annotation { "Feature Type Name" : "Feature", "Feature Type Description" : "" }
export const myFeature = defineFeature(function(context is Context, id is Id, definition is map)
    precondition{}
    {
        {
            var Q0;
            Q0=qCreatedBy(makeId("Top.planeOp"),FACE);
            var sketch = newSketch(context, id + "F0", { "sketchPlane" : qUnion([Q0])});
            skLineSegment(sketch, "E0.bottom", {"start": v(-60, -117) * mm, "end": v(60, -117) * mm});
            skLineSegment(sketch, "E0.left", {"start": v(-60, -117) * mm, "end": v(-60, 59) * mm});
            skLineSegment(sketch, "E0.right", {"start": v(60, -117) * mm, "end": v(60, 59) * mm});
            skLineSegment(sketch, "E1", {"start": v(-55, 63) * mm, "end": v(-30, 43) * mm});
            skLineSegment(sketch, "E2", {"start": v(-30, 43) * mm, "end": v(30, 43) * mm});
            skLineSegment(sketch, "E3", {"start": v(30, 43) * mm, "end": v(55, 63) * mm});
            skLineSegment(sketch, "E4", {"start": v(-30, 43) * mm, "end": v(-35, -47) * mm});
            skLineSegment(sketch, "E5", {"start": v(30, 43) * mm, "end": v(35, -47) * mm});
            skLineSegment(sketch, "E6", {"start": v(-60, 31) * mm, "end": v(-50, 23) * mm});
            skLineSegment(sketch, "E7", {"start": v(-60, -67) * mm, "end": v(-50, 23) * mm});
            skLineSegment(sketch, "E8", {"start": v(60, -67) * mm, "end": v(50, 23) * mm});
            skLineSegment(sketch, "E9", {"start": v(50, 23) * mm, "end": v(60, 31) * mm});
            skLineSegment(sketch, "E10", {"start": v(-56, 63) * mm, "end": v(-55, 63) * mm});
            skLineSegment(sketch, "E11", {"start": v(55, 63) * mm, "end": v(56, 63) * mm});
            skLineSegment(sketch, "E12", {"start": v(-51.28, -61) * mm, "end": v(-42.29, 19.96) * mm});
            skLineSegment(sketch, "E13", {"start": v(42.29, 19.96) * mm, "end": v(51.28, -61) * mm});
            skLineSegment(sketch, "E14", {"start": v(-51.28, -61) * mm, "end": v(-35, -47) * mm});
            skLineSegment(sketch, "E15", {"start": v(-42.29, 19.96) * mm, "end": v(-31.52, 15.65) * mm});
            skLineSegment(sketch, "E16", {"start": v(42.29, 19.96) * mm, "end": v(31.52, 15.65) * mm});
            skLineSegment(sketch, "E17", {"start": v(35, -47) * mm, "end": v(51.28, -61) * mm});
            skPoint(sketch, "E18.visualSharp", {"position": v(60, -117) * mm});
            skLineSegment(sketch, "E18.filletArc", {"start": v(60, -117) * mm, "end": v(60, -117) * mm});
            skPoint(sketch, "E19.visualSharp", {"position": v(-60, -117) * mm});
            skLineSegment(sketch, "E19.filletArc", {"start": v(-60, -117) * mm, "end": v(-60, -117) * mm});
            skPoint(sketch, "E20.visualSharp", {"position": v(-60, 63) * mm});
            skArc(sketch, "E20.filletArc", {"start": v(-56, 63) * mm, "mid": v(-58.83, 61.84) * mm, "end": v(-60, 59) * mm});
            skPoint(sketch, "E21.visualSharp", {"position": v(60, 63) * mm});
            skArc(sketch, "E21.filletArc", {"start": v(60, 59) * mm, "mid": v(58.83, 61.84) * mm, "end": v(56, 63) * mm});
            skPoint(sketch, "E22.endSnap0", {"position": v(-42.5, 53) * mm});
            skLineSegment(sketch, "E23", {"start": v(-52, 34.85) * mm, "end": v(-46, 30.05) * mm});
            skLineSegment(sketch, "E24", {"start": v(-52, 34.85) * mm, "end": v(-52, 50.36) * mm});
            skLineSegment(sketch, "E25", {"start": v(-52, 50.36) * mm, "end": v(-38.22, 39.34) * mm});
            skLineSegment(sketch, "E26", {"start": v(-38.22, 39.34) * mm, "end": v(-38.89, 27.21) * mm});
            skLineSegment(sketch, "E27", {"start": v(52, 50.36) * mm, "end": v(52, 34.85) * mm});
            skLineSegment(sketch, "E28", {"start": v(52, 34.85) * mm, "end": v(46, 30.05) * mm});
            skLineSegment(sketch, "E29", {"start": v(46, 30.05) * mm, "end": v(38.89, 27.21) * mm});
            skLineSegment(sketch, "E30", {"start": v(38.89, 27.21) * mm, "end": v(38.22, 39.34) * mm});
            skLineSegment(sketch, "E31", {"start": v(38.22, 39.34) * mm, "end": v(52, 50.36) * mm});
            skLineSegment(sketch, "E32", {"start": v(-46, 30.05) * mm, "end": v(-38.89, 27.21) * mm});
            skLineSegment(sketch, "E33", {"start": v(-51.28, -61) * mm, "end": v(-60, -67) * mm});
            skLineSegment(sketch, "E34", {"start": v(51.28, -61) * mm, "end": v(60, -67) * mm});
            skLineSegment(sketch, "E35", {"start": v(-58, -69.4) * mm, "end": v(-58, -115) * mm});
            skLineSegment(sketch, "E36", {"start": v(-58, -115) * mm, "end": v(58, -115) * mm});
            skLineSegment(sketch, "E37", {"start": v(58, -115) * mm, "end": v(58, -69.4) * mm});
            skLineSegment(sketch, "E38", {"start": v(28.1, 41) * mm, "end": v(-28.1, 41) * mm});
            skLineSegment(sketch, "E39", {"start": v(-28.1, 41) * mm, "end": v(-33.05, -47.95) * mm});
            skLineSegment(sketch, "E40", {"start": v(-33.05, -47.95) * mm, "end": v(-58, -69.4) * mm});
            skLineSegment(sketch, "E41", {"start": v(28.1, 41) * mm, "end": v(33.05, -47.95) * mm});
            skLineSegment(sketch, "E42", {"start": v(33.05, -47.95) * mm, "end": v(58, -69.4) * mm});
            skPoint(sketch, "E43.visualSharp", {"position": v(-58, -115) * mm});
            skLineSegment(sketch, "E43.filletArc", {"start": v(-58, -115) * mm, "end": v(-58, -115) * mm});
            skPoint(sketch, "E44.visualSharp", {"position": v(58, -115) * mm});
            skLineSegment(sketch, "E44.filletArc", {"start": v(58, -115) * mm, "end": v(58, -115) * mm});
            skLineSegment(sketch, "E45", {"start": v(-58, 29.4) * mm, "end": v(-58, 57.76) * mm});
            skLineSegment(sketch, "E46", {"start": v(-54, 61.76) * mm, "end": v(-53.44, 61.76) * mm});
            skPoint(sketch, "E47.visualSharp", {"position": v(-58, 61.76) * mm});
            skArc(sketch, "E47.filletArc", {"start": v(-54, 61.76) * mm, "mid": v(-56.83, 60.59) * mm, "end": v(-58, 57.76) * mm});
            skLineSegment(sketch, "E48", {"start": v(58, 29.4) * mm, "end": v(58, 57.76) * mm});
            skLineSegment(sketch, "E49", {"start": v(54, 61.76) * mm, "end": v(53.44, 61.76) * mm});
            skPoint(sketch, "E50.visualSharp", {"position": v(58, 61.76) * mm});
            skArc(sketch, "E50.filletArc", {"start": v(58, 57.76) * mm, "mid": v(56.83, 60.59) * mm, "end": v(54, 61.76) * mm});
            skSolve(sketch);
        }
        {
            var Q0;
            {var subQ9=sQuery(id+"F0.wireOp",EDGE,"E0.bottom");Q0=makeQuery(id+"F0.imprint","IMPRINT",FACE,{"disambiguationData":[TD([[makeQuery(id+"F0.imprint","IMPRINT",EDGE,{"derivedFrom":subQ9}),1.0]])]});}
            var Q1;
            Q1=makeQuery(id+"F0.imprint","IMPRINT",FACE,{"disambiguationData":[TD([[makeQuery(id+"F0.imprint","IMPRINT",EDGE,{"derivedFrom":sQuery(id+"F0.wireOp",EDGE,"E35")}),1.0]])]});
            var Q2;
            {var subQ0=sQuery(id+"F0.wireOp",EDGE,"E1");Q2=makeQuery(id+"F0.imprint","IMPRINT",FACE,{"disambiguationData":[TD([[makeQuery(id+"F0.imprint","IMPRINT",EDGE,{"derivedFrom":subQ0}),-1.0]])]});}
            var Q3;
            {var subQ4=sQuery(id+"F0.wireOp",EDGE,"E3");Q3=makeQuery(id+"F0.imprint","IMPRINT",FACE,{"disambiguationData":[TD([[makeQuery(id+"F0.imprint","IMPRINT",EDGE,{"derivedFrom":subQ4}),-1.0]])]});}
            var Q4;
            {var subQ6=sQuery(id+"F0.wireOp",EDGE,"E7");Q4=makeQuery(id+"F0.imprint","IMPRINT",FACE,{"disambiguationData":[TD([[makeQuery(id+"F0.imprint","IMPRINT",EDGE,{"derivedFrom":subQ6}),-1.0]])]});}
            var Q5;
            {var subQ6=sQuery(id+"F0.wireOp",EDGE,"E8");Q5=makeQuery(id+"F0.imprint","IMPRINT",FACE,{"disambiguationData":[TD([[makeQuery(id+"F0.imprint","IMPRINT",EDGE,{"derivedFrom":subQ6}),1.0]])]});}
            extrude(context, id + "F1", {"entities" : qUnion([Q0, Q1, Q2, Q3, Q4, Q5]), "depth" : 3 * mm, "offsetDistance" : 25 * mm});
        }
        {
            var Q0;
            Q0=makeQuery(id+"F0.imprint","IMPRINT",FACE,{"disambiguationData":[TD([[makeQuery(id+"F0.imprint","IMPRINT",EDGE,{"derivedFrom":sQuery(id+"F0.wireOp",EDGE,"E0.bottom")}),1.0]])]});
            var Q1;
            {var subQ0=sQuery(id+"F0.wireOp",EDGE,"E10");Q1=makeQuery(id+"F0.imprint","IMPRINT",FACE,{"disambiguationData":[TD([[makeQuery(id+"F0.imprint","IMPRINT",EDGE,{"derivedFrom":subQ0}),-1.0]])]});}
            var Q2;
            {var subQ0=sQuery(id+"F0.wireOp",EDGE,"E11");Q2=makeQuery(id+"F0.imprint","IMPRINT",FACE,{"disambiguationData":[TD([[makeQuery(id+"F0.imprint","IMPRINT",EDGE,{"derivedFrom":subQ0}),-1.0]])]});}
            extrude(context, id + "F2", {"entities" : qUnion([Q0, Q1, Q2]), "operationType" : NewBodyOperationType.ADD, "depth" : 32 * mm, "offsetDistance" : 25 * mm});
        }
        {
            var Q0;
            Q0=makeQuery(id+"F1.opExtrude","CAP_EDGE",EDGE,{"disambiguationData":[OSD([sQuery(id+"F0.wireOp",EDGE,"E8")])],"isStart":false});
            var Q1;
            Q1=makeQuery(id+"F1.opExtrude","CAP_EDGE",EDGE,{"disambiguationData":[OSD([sQuery(id+"F0.wireOp",EDGE,"E8")])],"isStart":true});
            var Q2;
            Q2=makeQuery(id+"F1.opExtrude","CAP_EDGE",EDGE,{"disambiguationData":[OSD([sQuery(id+"F0.wireOp",EDGE,"E13")])],"isStart":false});
            var Q3;
            Q3=makeQuery(id+"F1.opExtrude","CAP_EDGE",EDGE,{"disambiguationData":[OSD([sQuery(id+"F0.wireOp",EDGE,"E16")])],"isStart":false});
            var Q4;
            Q4=makeQuery(id+"F1.opExtrude","CAP_EDGE",EDGE,{"disambiguationData":[OSD([sQuery(id+"F0.wireOp",EDGE,"E9")])],"isStart":true});
            var Q5;
            Q5=makeQuery(id+"F1.opExtrude","CAP_EDGE",EDGE,{"disambiguationData":[OSD([sQuery(id+"F0.wireOp",EDGE,"E29")])],"isStart":false});
            var Q6;
            Q6=makeQuery(id+"F1.opExtrude","CAP_EDGE",EDGE,{"disambiguationData":[OSD([sQuery(id+"F0.wireOp",EDGE,"E30")])],"isStart":false});
            var Q7;
            Q7=makeQuery(id+"F1.opExtrude","CAP_EDGE",EDGE,{"disambiguationData":[OSD([sQuery(id+"F0.wireOp",EDGE,"E31")])],"isStart":false});
            var Q8;
            Q8=makeQuery(id+"F1.opExtrude","CAP_EDGE",EDGE,{"disambiguationData":[OSD([sQuery(id+"F0.wireOp",EDGE,"E27")])],"isStart":false});
            var Q9;
            Q9=makeQuery(id+"F1.opExtrude","CAP_EDGE",EDGE,{"disambiguationData":[OSD([sQuery(id+"F0.wireOp",EDGE,"E28")])],"isStart":false});
            var Q10;
            Q10=makeQuery(id+"F1.opExtrude","CAP_EDGE",EDGE,{"disambiguationData":[OSD([sQuery(id+"F0.wireOp",EDGE,"E3")])],"isStart":false});
            var Q11;
            Q11=makeQuery(id+"F1.opExtrude","CAP_EDGE",EDGE,{"disambiguationData":[OSD([sQuery(id+"F0.wireOp",EDGE,"E9")])],"isStart":false});
            var Q12;
            Q12=makeQuery(id+"F1.opExtrude","CAP_EDGE",EDGE,{"disambiguationData":[OSD([sQuery(id+"F0.wireOp",EDGE,"E13")])],"isStart":true});
            var Q13;
            {var subQ0=sQuery(id+"F0.wireOp",EDGE,"E0.right");Q13=makeQuery(id+"F1.opExtrude","CAP_EDGE",EDGE,{"disambiguationData":[OSD([subQ0]),TDD([makeQuery(id+"F0.imprint","IMPRINT",EDGE,{"disambiguationData":[TD([[makeQuery(id+"F0.imprint","INTERSECT",VERTEX,{"derivedFrom":[subQ0,sQuery(id+"F0.wireOp",EDGE,"E21.filletArc")]}),1.0]])],"derivedFrom":subQ0})])],"isStart":true});}
            var Q14;
            Q14=makeQuery(id+"F1.opExtrude","CAP_EDGE",EDGE,{"disambiguationData":[OSD([sQuery(id+"F0.wireOp",EDGE,"E21.filletArc")])],"isStart":true});
            var Q15;
            Q15=makeQuery(id+"F1.opExtrude","CAP_EDGE",EDGE,{"disambiguationData":[OSD([sQuery(id+"F0.wireOp",EDGE,"E3")])],"isStart":true});
            var Q16;
            Q16=makeQuery(id+"F1.opExtrude","CAP_EDGE",EDGE,{"disambiguationData":[OSD([sQuery(id+"F0.wireOp",EDGE,"E27")])],"isStart":true});
            var Q17;
            Q17=makeQuery(id+"F1.opExtrude","CAP_EDGE",EDGE,{"disambiguationData":[OSD([sQuery(id+"F0.wireOp",EDGE,"E31")])],"isStart":true});
            var Q18;
            Q18=makeQuery(id+"F1.opExtrude","CAP_EDGE",EDGE,{"disambiguationData":[OSD([sQuery(id+"F0.wireOp",EDGE,"E29")])],"isStart":true});
            var Q19;
            Q19=makeQuery(id+"F1.opExtrude","CAP_EDGE",EDGE,{"disambiguationData":[OSD([sQuery(id+"F0.wireOp",EDGE,"E28")])],"isStart":true});
            var Q20;
            Q20=makeQuery(id+"F1.opExtrude","CAP_EDGE",EDGE,{"disambiguationData":[OSD([sQuery(id+"F0.wireOp",EDGE,"E30")])],"isStart":true});
            var Q21;
            Q21=makeQuery(id+"F1.opExtrude","CAP_EDGE",EDGE,{"disambiguationData":[OSD([sQuery(id+"F0.wireOp",EDGE,"E26")])],"isStart":false});
            var Q22;
            Q22=makeQuery(id+"F1.opExtrude","CAP_EDGE",EDGE,{"disambiguationData":[OSD([sQuery(id+"F0.wireOp",EDGE,"E32")])],"isStart":false});
            var Q23;
            Q23=makeQuery(id+"F1.opExtrude","CAP_EDGE",EDGE,{"disambiguationData":[OSD([sQuery(id+"F0.wireOp",EDGE,"E23")])],"isStart":false});
            var Q24;
            Q24=makeQuery(id+"F1.opExtrude","CAP_EDGE",EDGE,{"disambiguationData":[OSD([sQuery(id+"F0.wireOp",EDGE,"E24")])],"isStart":false});
            var Q25;
            Q25=makeQuery(id+"F1.opExtrude","CAP_EDGE",EDGE,{"disambiguationData":[OSD([sQuery(id+"F0.wireOp",EDGE,"E25")])],"isStart":false});
            var Q26;
            Q26=makeQuery(id+"F1.opExtrude","CAP_EDGE",EDGE,{"disambiguationData":[OSD([sQuery(id+"F0.wireOp",EDGE,"E1")])],"isStart":false});
            var Q27;
            Q27=makeQuery(id+"F1.opExtrude","CAP_EDGE",EDGE,{"disambiguationData":[OSD([sQuery(id+"F0.wireOp",EDGE,"E15")])],"isStart":false});
            var Q28;
            Q28=makeQuery(id+"F1.opExtrude","CAP_EDGE",EDGE,{"disambiguationData":[OSD([sQuery(id+"F0.wireOp",EDGE,"E7")])],"isStart":false});
            var Q29;
            Q29=makeQuery(id+"F1.opExtrude","CAP_EDGE",EDGE,{"disambiguationData":[OSD([sQuery(id+"F0.wireOp",EDGE,"E12")])],"isStart":false});
            var Q30;
            Q30=makeQuery(id+"F1.opExtrude","CAP_EDGE",EDGE,{"disambiguationData":[OSD([sQuery(id+"F0.wireOp",EDGE,"E6")])],"isStart":false});
            var Q31;
            Q31=makeQuery(id+"F1.opExtrude","CAP_EDGE",EDGE,{"disambiguationData":[OSD([sQuery(id+"F0.wireOp",EDGE,"E12")])],"isStart":true});
            var Q32;
            Q32=makeQuery(id+"F1.opExtrude","CAP_EDGE",EDGE,{"disambiguationData":[OSD([sQuery(id+"F0.wireOp",EDGE,"E7")])],"isStart":true});
            var Q33;
            {var subQ0=sQuery(id+"F0.wireOp",EDGE,"E0.left");Q33=makeQuery(id+"F1.opExtrude","CAP_EDGE",EDGE,{"disambiguationData":[OSD([subQ0]),TDD([makeQuery(id+"F0.imprint","IMPRINT",EDGE,{"disambiguationData":[TD([[makeQuery(id+"F0.imprint","INTERSECT",VERTEX,{"derivedFrom":[subQ0,sQuery(id+"F0.wireOp",EDGE,"E20.filletArc")]}),1.0]])],"derivedFrom":subQ0})])],"isStart":true});}
            var Q34;
            Q34=makeQuery(id+"F1.opExtrude","CAP_EDGE",EDGE,{"disambiguationData":[OSD([sQuery(id+"F0.wireOp",EDGE,"E20.filletArc")])],"isStart":true});
            var Q35;
            Q35=makeQuery(id+"F1.opExtrude","CAP_EDGE",EDGE,{"disambiguationData":[OSD([sQuery(id+"F0.wireOp",EDGE,"E26")])],"isStart":true});
            var Q36;
            Q36=makeQuery(id+"F1.opExtrude","CAP_EDGE",EDGE,{"disambiguationData":[OSD([sQuery(id+"F0.wireOp",EDGE,"E25")])],"isStart":true});
            var Q37;
            Q37=makeQuery(id+"F1.opExtrude","CAP_EDGE",EDGE,{"disambiguationData":[OSD([sQuery(id+"F0.wireOp",EDGE,"E24")])],"isStart":true});
            var Q38;
            Q38=makeQuery(id+"F1.opExtrude","CAP_EDGE",EDGE,{"disambiguationData":[OSD([sQuery(id+"F0.wireOp",EDGE,"E6")])],"isStart":true});
            var Q39;
            Q39=makeQuery(id+"F1.opExtrude","CAP_EDGE",EDGE,{"disambiguationData":[OSD([sQuery(id+"F0.wireOp",EDGE,"E15")])],"isStart":true});
            var Q40;
            Q40=makeQuery(id+"F1.opExtrude","CAP_EDGE",EDGE,{"disambiguationData":[OSD([sQuery(id+"F0.wireOp",EDGE,"E32")])],"isStart":true});
            var Q41;
            Q41=makeQuery(id+"F1.opExtrude","CAP_EDGE",EDGE,{"disambiguationData":[OSD([sQuery(id+"F0.wireOp",EDGE,"E23")])],"isStart":true});
            fillet(context, id + "F3", {"entities" : qUnion([Q0, Q1, Q2, Q3, Q4, Q5, Q6, Q7, Q8, Q9, Q10, Q11, Q12, Q13, Q14, Q15, Q16, Q17, Q18, Q19, Q20, Q21, Q22, Q23, Q24, Q25, Q26, Q27, Q28, Q29, Q30, Q31, Q32, Q33, Q34, Q35, Q36, Q37, Q38, Q39, Q40, Q41]), "radius" : 1 * mm, "tangentPropagation" : true, "allowEdgeOverflow" : false});
        }
        {
            var Q0;
            {var subQ0=sQuery(id+"F0.wireOp",EDGE,"E0.right");var subQ1=makeQuery(id+"F0.imprint","IMPRINT",EDGE,{"disambiguationData":[TD([[makeQuery(id+"F0.imprint","INTERSECT",VERTEX,{"derivedFrom":[sQuery(id+"F0.wireOp",EDGE,"E0.bottom"),subQ0]}),-1.0]])],"derivedFrom":subQ0});Q0=makeQuery(id+"F2.boolean.opBoolean","MERGE",FACE,{"derivedFrom":[makeQuery(id+"F1.opExtrude","SWEPT_FACE",FACE,{"disambiguationData":[OSD([subQ0]),TDD([subQ1])]}),makeQuery(id+"F2.opExtrude","SWEPT_FACE",FACE,{"disambiguationData":[OSD([subQ0]),TDD([subQ1])]})]});}
            var sketch = newSketch(context, id + "F4", { "sketchPlane" : qUnion([Q0])});
            skCircle(sketch, "E51", {"center": v(-102.24, 15.75) * mm, "radius": 13 * mm});
            skLineSegment(sketch, "E52.bottom", {"start": v(-117, 0) * mm, "end": v(-84.5, 0) * mm});
            skLineSegment(sketch, "E52.top", {"start": v(-117, 11.75) * mm, "end": v(-84.5, 11.75) * mm});
            skLineSegment(sketch, "E52.left", {"start": v(-117, 0) * mm, "end": v(-117, 11.75) * mm});
            skLineSegment(sketch, "E52.right", {"start": v(-84.5, 0) * mm, "end": v(-84.5, 11.75) * mm});
            skCircle(sketch, "E53", {"center": v(-102.24, 15.75) * mm, "radius": 3.5 * mm});
            skCircle(sketch, "E54", {"center": v(-110.74, 15.75) * mm, "radius": 1.5 * mm});
            skCircle(sketch, "E55", {"center": v(-93.74, 15.75) * mm, "radius": 1.5 * mm});
            skSolve(sketch);
        }
        {
            var Q0;
            Q0=makeQuery(id+"F4.imprint","IMPRINT",FACE,{"disambiguationData":[TD([[makeQuery(id+"F4.imprint","IMPRINT",EDGE,{"derivedFrom":sQuery(id+"F4.wireOp",EDGE,"E52.bottom")}),1.0]])]});
            extrude(context, id + "F5", {"entities" : qUnion([Q0]), "operationType" : NewBodyOperationType.ADD, "oppositeDirection" : true, "depth" : 120 * mm, "offsetDistance" : 25 * mm});
        }
        {
            var Q0;
            Q0=makeQuery(id+"F4.imprint","IMPRINT",FACE,{"disambiguationData":[TD([[makeQuery(id+"F4.imprint","IMPRINT",EDGE,{"derivedFrom":sQuery(id+"F4.wireOp",EDGE,"E54")}),1.0]])]});
            var Q1;
            Q1=makeQuery(id+"F4.imprint","IMPRINT",FACE,{"disambiguationData":[TD([[makeQuery(id+"F4.imprint","IMPRINT",EDGE,{"derivedFrom":sQuery(id+"F4.wireOp",EDGE,"E53")}),1.0]])]});
            var Q2;
            Q2=makeQuery(id+"F4.imprint","IMPRINT",FACE,{"disambiguationData":[TD([[makeQuery(id+"F4.imprint","IMPRINT",EDGE,{"derivedFrom":sQuery(id+"F4.wireOp",EDGE,"E55")}),1.0]])]});
            extrude(context, id + "F6", {"entities" : qUnion([Q0, Q1, Q2]), "operationType" : NewBodyOperationType.REMOVE, "oppositeDirection" : true, "depth" : 150 * mm, "offsetDistance" : 25 * mm});
        }
        {
            var Q0;
            Q0=makeQuery(id+"F5.opExtrude","SWEPT_FACE",FACE,{"disambiguationData":[OSD([sQuery(id+"F4.wireOp",EDGE,"E52.right")])]});
            var sketch = newSketch(context, id + "F7", { "sketchPlane" : qUnion([Q0])});
            skLineSegment(sketch, "E56.bottom", {"start": v(40, 11.75) * mm, "end": v(-40, 11.75) * mm});
            skLineSegment(sketch, "E56.top", {"start": v(40, 3) * mm, "end": v(-40, 3) * mm});
            skLineSegment(sketch, "E56.left", {"start": v(40, 11.75) * mm, "end": v(40, 3) * mm});
            skLineSegment(sketch, "E56.right", {"start": v(-40, 11.75) * mm, "end": v(-40, 3) * mm});
            skSolve(sketch);
        }
        {
            var Q0;
            Q0 = qSketchRegion(id + "F7", true);
            extrude(context, id + "F8", {"entities" : qUnion([Q0]), "operationType" : NewBodyOperationType.REMOVE, "oppositeDirection" : true, "depth" : 30.5 * mm, "offsetDistance" : 25 * mm});
        }
        {
            var Q0;
            Q0=makeQuery(id+"F2.opExtrude","CAP_FACE",FACE,{"disambiguationData":[OSD([sQuery(id+"F0.wireOp",EDGE,"E0.bottom"),sQuery(id+"F0.wireOp",EDGE,"E0.left"),sQuery(id+"F0.wireOp",EDGE,"E0.right"),sQuery(id+"F0.wireOp",EDGE,"E2"),sQuery(id+"F0.wireOp",EDGE,"E4"),sQuery(id+"F0.wireOp",EDGE,"E5"),sQuery(id+"F0.wireOp",EDGE,"E14"),sQuery(id+"F0.wireOp",EDGE,"E17"),sQuery(id+"F0.wireOp",EDGE,"E33"),sQuery(id+"F0.wireOp",EDGE,"E34"),sQuery(id+"F0.wireOp",EDGE,"E35"),sQuery(id+"F0.wireOp",EDGE,"E36"),sQuery(id+"F0.wireOp",EDGE,"E37"),sQuery(id+"F0.wireOp",EDGE,"E38"),sQuery(id+"F0.wireOp",EDGE,"E39"),sQuery(id+"F0.wireOp",EDGE,"E40"),sQuery(id+"F0.wireOp",EDGE,"E41"),sQuery(id+"F0.wireOp",EDGE,"E42")])],"isStart":false});
            var sketch = newSketch(context, id + "F9", { "sketchPlane" : qUnion([Q0])});
            skLineSegment(sketch, "E57.bottom", {"start": v(60, -85) * mm, "end": v(66, -85) * mm});
            skLineSegment(sketch, "E57.top", {"start": v(60, -79) * mm, "end": v(66, -79) * mm});
            skLineSegment(sketch, "E57.left", {"start": v(60, -85) * mm, "end": v(60, -79) * mm});
            skLineSegment(sketch, "E57.right", {"start": v(66, -85) * mm, "end": v(66, -79) * mm});
            skLineSegment(sketch, "E58", {"start": v(60, -117) * mm, "end": v(60, 63.09) * mm, "construction": true});
            skLineSegment(sketch, "E59.bottom", {"start": v(60, -73) * mm, "end": v(66, -73) * mm});
            skLineSegment(sketch, "E59.top", {"start": v(60, -59) * mm, "end": v(66, -59) * mm});
            skLineSegment(sketch, "E59.left", {"start": v(60, -73) * mm, "end": v(60, -59) * mm});
            skLineSegment(sketch, "E59.right", {"start": v(66, -73) * mm, "end": v(66, -59) * mm});
            skLineSegment(sketch, "E60.bottom", {"start": v(60, -53) * mm, "end": v(66, -53) * mm});
            skLineSegment(sketch, "E60.top", {"start": v(60, -47) * mm, "end": v(66, -47) * mm});
            skLineSegment(sketch, "E60.left", {"start": v(60, -53) * mm, "end": v(60, -47) * mm});
            skLineSegment(sketch, "E60.right", {"start": v(66, -53) * mm, "end": v(66, -47) * mm});
            skLineSegment(sketch, "E61", {"start": v(60, -59) * mm, "end": v(60, -53) * mm});
            skLineSegment(sketch, "E62.bottom", {"start": v(60, 57) * mm, "end": v(66, 57) * mm});
            skLineSegment(sketch, "E62.top", {"start": v(60, 43) * mm, "end": v(66, 43) * mm});
            skLineSegment(sketch, "E62.left", {"start": v(60, 57) * mm, "end": v(60, 43) * mm});
            skLineSegment(sketch, "E62.right", {"start": v(66, 57) * mm, "end": v(66, 43) * mm});
            skLineSegment(sketch, "E63.bottom", {"start": v(60, 31) * mm, "end": v(66, 31) * mm});
            skLineSegment(sketch, "E63.top", {"start": v(60, 37) * mm, "end": v(66, 37) * mm});
            skLineSegment(sketch, "E63.left", {"start": v(60, 31) * mm, "end": v(60, 37) * mm});
            skLineSegment(sketch, "E63.right", {"start": v(66, 31) * mm, "end": v(66, 37) * mm});
            skLineSegment(sketch, "E64.bottom", {"start": v(-60, -85) * mm, "end": v(-66, -85) * mm});
            skLineSegment(sketch, "E64.top", {"start": v(-60, -79) * mm, "end": v(-66, -79) * mm});
            skLineSegment(sketch, "E64.left", {"start": v(-60, -85) * mm, "end": v(-60, -79) * mm});
            skLineSegment(sketch, "E64.right", {"start": v(-66, -85) * mm, "end": v(-66, -79) * mm});
            skLineSegment(sketch, "E65.bottom", {"start": v(-60, -73) * mm, "end": v(-66, -73) * mm});
            skLineSegment(sketch, "E65.top", {"start": v(-60, -59) * mm, "end": v(-66, -59) * mm});
            skLineSegment(sketch, "E65.left", {"start": v(-60, -73) * mm, "end": v(-60, -59) * mm});
            skLineSegment(sketch, "E65.right", {"start": v(-66, -73) * mm, "end": v(-66, -59) * mm});
            skLineSegment(sketch, "E66", {"start": v(-60, -117) * mm, "end": v(-60, 63.33) * mm, "construction": true});
            skPoint(sketch, "E67.visualSharp", {"position": v(66, -47) * mm});
            skLineSegment(sketch, "E67.filletArc", {"start": v(66, -47) * mm, "end": v(66, -47) * mm});
            skLineSegment(sketch, "E68", {"start": v(60, -47) * mm, "end": v(58, -47) * mm});
            skLineSegment(sketch, "E69", {"start": v(58, -47) * mm, "end": v(48.22, -58.36) * mm});
            skLineSegment(sketch, "E70.bottom", {"start": v(-60, -53) * mm, "end": v(-66, -53) * mm});
            skLineSegment(sketch, "E70.top", {"start": v(-60, -47) * mm, "end": v(-66, -47) * mm});
            skLineSegment(sketch, "E70.left", {"start": v(-60, -53) * mm, "end": v(-60, -47) * mm});
            skLineSegment(sketch, "E70.right", {"start": v(-66, -53) * mm, "end": v(-66, -47) * mm});
            skLineSegment(sketch, "E71", {"start": v(-60, -59) * mm, "end": v(-60, -53) * mm});
            skLineSegment(sketch, "E72", {"start": v(-60, -47) * mm, "end": v(-58, -47) * mm});
            skLineSegment(sketch, "E73", {"start": v(-58, -47) * mm, "end": v(-48.22, -58.36) * mm});
            skPoint(sketch, "E74.visualSharp", {"position": v(-66, -47) * mm});
            skLineSegment(sketch, "E74.filletArc", {"start": v(-66, -47) * mm, "end": v(-66, -47) * mm});
            skLineSegment(sketch, "E75.bottom", {"start": v(-60, 31) * mm, "end": v(-66, 31) * mm});
            skLineSegment(sketch, "E75.top", {"start": v(-60, 37) * mm, "end": v(-66, 37) * mm});
            skLineSegment(sketch, "E75.left", {"start": v(-60, 31) * mm, "end": v(-60, 37) * mm});
            skLineSegment(sketch, "E75.right", {"start": v(-66, 31) * mm, "end": v(-66, 37) * mm});
            skLineSegment(sketch, "E76.bottom", {"start": v(-60, 43) * mm, "end": v(-66, 43) * mm});
            skLineSegment(sketch, "E76.top", {"start": v(-60, 57) * mm, "end": v(-66, 57) * mm});
            skLineSegment(sketch, "E76.left", {"start": v(-60, 43) * mm, "end": v(-60, 57) * mm});
            skLineSegment(sketch, "E76.right", {"start": v(-66, 43) * mm, "end": v(-66, 57) * mm});
            skSolve(sketch);
        }
        {
            var Q0;
            {var subQ7=sQuery(id+"F9.wireOp",EDGE,"E59.left");Q0=makeQuery(id+"F9.imprint","IMPRINT",FACE,{"disambiguationData":[TD([[makeQuery(id+"F9.imprint","IMPRINT",EDGE,{"derivedFrom":subQ7}),1.0]])]});}
            var Q1;
            Q1=makeQuery(id+"F9.imprint","IMPRINT",FACE,{"disambiguationData":[TD([[makeQuery(id+"F9.imprint","IMPRINT",EDGE,{"derivedFrom":sQuery(id+"F9.wireOp",EDGE,"E60.bottom")}),1.0]])]});
            var Q2;
            Q2=makeQuery(id+"F9.imprint","IMPRINT",FACE,{"disambiguationData":[TD([[makeQuery(id+"F9.imprint","IMPRINT",EDGE,{"derivedFrom":sQuery(id+"F9.wireOp",EDGE,"E59.bottom")}),1.0]])]});
            var Q3;
            {var subQ5=sQuery(id+"F9.wireOp",EDGE,"I04EUQrT-3LK4-v9OJ-XVl4-QNwkVvTIr2Wa.bottom");Q3=makeQuery(id+"F9.imprint","IMPRINT",FACE,{"disambiguationData":[TD([[makeQuery(id+"F9.imprint","IMPRINT",EDGE,{"derivedFrom":subQ5}),1.0]])]});}
            var Q4;
            Q4=makeQuery(id+"F9.imprint","IMPRINT",FACE,{"disambiguationData":[TD([[makeQuery(id+"F9.imprint","IMPRINT",EDGE,{"derivedFrom":sQuery(id+"F9.wireOp",EDGE,"E57.bottom")}),1.0]])]});
            var Q5;
            Q5=makeQuery(id+"F9.imprint","IMPRINT",FACE,{"disambiguationData":[TD([[makeQuery(id+"F9.imprint","IMPRINT",EDGE,{"derivedFrom":sQuery(id+"F9.wireOp",EDGE,"E63.bottom")}),1.0]])]});
            var Q6;
            Q6=makeQuery(id+"F9.imprint","IMPRINT",FACE,{"disambiguationData":[TD([[makeQuery(id+"F9.imprint","IMPRINT",EDGE,{"derivedFrom":sQuery(id+"F9.wireOp",EDGE,"E62.bottom")}),-1.0]])]});
            var Q7;
            Q7=makeQuery(id+"F9.imprint","IMPRINT",FACE,{"disambiguationData":[TD([[makeQuery(id+"F9.imprint","IMPRINT",EDGE,{"derivedFrom":sQuery(id+"F9.wireOp",EDGE,"E64.bottom")}),-1.0]])]});
            var Q8;
            {var subQ4=sQuery(id+"F9.wireOp",EDGE,"E65.bottom");Q8=makeQuery(id+"F9.imprint","IMPRINT",FACE,{"disambiguationData":[TD([[makeQuery(id+"F9.imprint","IMPRINT",EDGE,{"derivedFrom":subQ4}),-1.0]])]});}
            var Q9;
            Q9=makeQuery(id+"F9.imprint","IMPRINT",FACE,{"disambiguationData":[TD([[makeQuery(id+"F9.imprint","IMPRINT",EDGE,{"derivedFrom":sQuery(id+"F9.wireOp",EDGE,"E70.left")}),-1.0]])]});
            var Q10;
            Q10=makeQuery(id+"F9.imprint","IMPRINT",FACE,{"disambiguationData":[TD([[makeQuery(id+"F9.imprint","IMPRINT",EDGE,{"derivedFrom":sQuery(id+"F9.wireOp",EDGE,"E70.bottom")}),-1.0]])]});
            var Q11;
            Q11=makeQuery(id+"F9.imprint","IMPRINT",FACE,{"disambiguationData":[TD([[makeQuery(id+"F9.imprint","IMPRINT",EDGE,{"derivedFrom":sQuery(id+"F9.wireOp",EDGE,"E75.bottom")}),-1.0]])]});
            var Q12;
            Q12=makeQuery(id+"F9.imprint","IMPRINT",FACE,{"disambiguationData":[TD([[makeQuery(id+"F9.imprint","IMPRINT",EDGE,{"derivedFrom":sQuery(id+"F9.wireOp",EDGE,"E76.bottom")}),-1.0]])]});
            extrude(context, id + "F10", {"entities" : qUnion([Q0, Q1, Q2, Q3, Q4, Q5, Q6, Q7, Q8, Q9, Q10, Q11, Q12]), "oppositeDirection" : true, "depth" : 6 * mm, "offsetDistance" : 25 * mm});
        }
        {
            var Q0;
            Q0=makeQuery(id+"F1.opExtrude","CAP_FACE",FACE,{"disambiguationData":[OSD([sQuery(id+"F0.wireOp",EDGE,"E0.bottom"),sQuery(id+"F0.wireOp",EDGE,"E0.left"),sQuery(id+"F0.wireOp",EDGE,"E0.right"),sQuery(id+"F0.wireOp",EDGE,"E1"),sQuery(id+"F0.wireOp",EDGE,"E2"),sQuery(id+"F0.wireOp",EDGE,"E3"),sQuery(id+"F0.wireOp",EDGE,"E4"),sQuery(id+"F0.wireOp",EDGE,"E5"),sQuery(id+"F0.wireOp",EDGE,"E6"),sQuery(id+"F0.wireOp",EDGE,"E7"),sQuery(id+"F0.wireOp",EDGE,"E8"),sQuery(id+"F0.wireOp",EDGE,"E9"),sQuery(id+"F0.wireOp",EDGE,"E10"),sQuery(id+"F0.wireOp",EDGE,"E11"),sQuery(id+"F0.wireOp",EDGE,"E12"),sQuery(id+"F0.wireOp",EDGE,"E13"),sQuery(id+"F0.wireOp",EDGE,"E14"),sQuery(id+"F0.wireOp",EDGE,"E15"),sQuery(id+"F0.wireOp",EDGE,"E16"),sQuery(id+"F0.wireOp",EDGE,"E17"),sQuery(id+"F0.wireOp",EDGE,"E20.filletArc"),sQuery(id+"F0.wireOp",EDGE,"E21.filletArc"),sQuery(id+"F0.wireOp",EDGE,"E23"),sQuery(id+"F0.wireOp",EDGE,"E24"),sQuery(id+"F0.wireOp",EDGE,"E25"),sQuery(id+"F0.wireOp",EDGE,"E26"),sQuery(id+"F0.wireOp",EDGE,"E27"),sQuery(id+"F0.wireOp",EDGE,"E28"),sQuery(id+"F0.wireOp",EDGE,"E29"),sQuery(id+"F0.wireOp",EDGE,"E30"),sQuery(id+"F0.wireOp",EDGE,"E31"),sQuery(id+"F0.wireOp",EDGE,"E32")])],"isStart":true});
            var sketch = newSketch(context, id + "F11", { "sketchPlane" : qUnion([Q0])});
            skLineSegment(sketch, "E77", {"start": v(-60, 117) * mm, "end": v(-60, -63.05) * mm, "construction": true});
            skLineSegment(sketch, "E78", {"start": v(60, 117) * mm, "end": v(60, -62.25) * mm, "construction": true});
            skLineSegment(sketch, "E79.bottom", {"start": v(-60, 75) * mm, "end": v(-66, 75) * mm});
            skLineSegment(sketch, "E79.top", {"start": v(-60, 69) * mm, "end": v(-66, 69) * mm});
            skLineSegment(sketch, "E79.left", {"start": v(-60, 75) * mm, "end": v(-60, 69) * mm});
            skLineSegment(sketch, "E79.right", {"start": v(-66, 75) * mm, "end": v(-66, 69) * mm});
            skLineSegment(sketch, "E80.bottom", {"start": v(-60, 57) * mm, "end": v(-66, 57) * mm});
            skLineSegment(sketch, "E80.top", {"start": v(-60, 63) * mm, "end": v(-66, 63) * mm});
            skLineSegment(sketch, "E80.left", {"start": v(-60, 57) * mm, "end": v(-60, 63) * mm});
            skLineSegment(sketch, "E80.right", {"start": v(-66, 57) * mm, "end": v(-66, 63) * mm});
            skLineSegment(sketch, "E81", {"start": v(-60, 57) * mm, "end": v(-60, 55.98) * mm});
            skLineSegment(sketch, "E82", {"start": v(-60, 76.05) * mm, "end": v(-60, 63) * mm});
            skLineSegment(sketch, "E83.bottom", {"start": v(-60, -41) * mm, "end": v(-66, -41) * mm});
            skLineSegment(sketch, "E83.top", {"start": v(-60, -47) * mm, "end": v(-66, -47) * mm});
            skLineSegment(sketch, "E83.left", {"start": v(-60, -41) * mm, "end": v(-60, -47) * mm});
            skLineSegment(sketch, "E83.right", {"start": v(-66, -41) * mm, "end": v(-66, -47) * mm});
            skLineSegment(sketch, "E84.bottom", {"start": v(-60, -53) * mm, "end": v(-66, -53) * mm});
            skLineSegment(sketch, "E84.top", {"start": v(-60, -59) * mm, "end": v(-66, -59) * mm});
            skLineSegment(sketch, "E84.left", {"start": v(-60, -53) * mm, "end": v(-60, -59) * mm});
            skLineSegment(sketch, "E84.right", {"start": v(-66, -53) * mm, "end": v(-66, -59) * mm});
            skLineSegment(sketch, "E85", {"start": v(-60, -47) * mm, "end": v(-59, -47) * mm});
            skLineSegment(sketch, "E86", {"start": v(-60, -53) * mm, "end": v(-59, -53) * mm});
            skLineSegment(sketch, "E87", {"start": v(-60, -59) * mm, "end": v(-59, -59) * mm});
            skLineSegment(sketch, "E88", {"start": v(-59, -59) * mm, "end": v(-59, -53) * mm});
            skLineSegment(sketch, "E89", {"start": v(-59, -47) * mm, "end": v(-59, -31.49) * mm});
            skLineSegment(sketch, "E90.bottom", {"start": v(60, 75) * mm, "end": v(66, 75) * mm});
            skLineSegment(sketch, "E90.top", {"start": v(60, 69) * mm, "end": v(66, 69) * mm});
            skLineSegment(sketch, "E90.left", {"start": v(60, 75) * mm, "end": v(60, 69) * mm});
            skLineSegment(sketch, "E90.right", {"start": v(66, 75) * mm, "end": v(66, 69) * mm});
            skLineSegment(sketch, "E91.bottom", {"start": v(60, 63) * mm, "end": v(66, 63) * mm});
            skLineSegment(sketch, "E91.top", {"start": v(60, 57) * mm, "end": v(66, 57) * mm});
            skLineSegment(sketch, "E91.left", {"start": v(60, 63) * mm, "end": v(60, 57) * mm});
            skLineSegment(sketch, "E91.right", {"start": v(66, 63) * mm, "end": v(66, 57) * mm});
            skLineSegment(sketch, "E92", {"start": v(60, 53) * mm, "end": v(60, 57) * mm});
            skLineSegment(sketch, "E93", {"start": v(60, 63) * mm, "end": v(60, 76.05) * mm});
            skLineSegment(sketch, "E94.bottom", {"start": v(60, -41) * mm, "end": v(66, -41) * mm});
            skLineSegment(sketch, "E94.top", {"start": v(60, -47) * mm, "end": v(66, -47) * mm});
            skLineSegment(sketch, "E94.left", {"start": v(60, -41) * mm, "end": v(60, -47) * mm});
            skLineSegment(sketch, "E94.right", {"start": v(66, -41) * mm, "end": v(66, -47) * mm});
            skLineSegment(sketch, "E95.bottom", {"start": v(60, -53) * mm, "end": v(66, -53) * mm});
            skLineSegment(sketch, "E95.top", {"start": v(60, -59) * mm, "end": v(66, -59) * mm});
            skLineSegment(sketch, "E95.left", {"start": v(60, -53) * mm, "end": v(60, -59) * mm});
            skLineSegment(sketch, "E95.right", {"start": v(66, -53) * mm, "end": v(66, -59) * mm});
            skLineSegment(sketch, "E96", {"start": v(59, -31.49) * mm, "end": v(59, -47) * mm});
            skLineSegment(sketch, "E97", {"start": v(59, -47) * mm, "end": v(60, -47) * mm});
            skLineSegment(sketch, "E98", {"start": v(60, -53) * mm, "end": v(59, -53) * mm});
            skLineSegment(sketch, "E99", {"start": v(59, -53) * mm, "end": v(59, -59) * mm});
            skLineSegment(sketch, "E100", {"start": v(59, -59) * mm, "end": v(60, -59) * mm});
            skLineSegment(sketch, "E101", {"start": v(60, 75) * mm, "end": v(60, 76.05) * mm});
            skLineSegment(sketch, "E102", {"start": v(60, 57) * mm, "end": v(51.85, 57) * mm});
            skLineSegment(sketch, "E103", {"start": v(51.85, 57) * mm, "end": v(52.51, 63) * mm});
            skLineSegment(sketch, "E104", {"start": v(52.51, 63) * mm, "end": v(58.55, 63) * mm});
            skLineSegment(sketch, "E105", {"start": v(58.55, 63) * mm, "end": v(60, 76.05) * mm});
            skLineSegment(sketch, "E106", {"start": v(-60, 57) * mm, "end": v(-51.85, 57) * mm});
            skLineSegment(sketch, "E107", {"start": v(-51.85, 57) * mm, "end": v(-52.51, 63) * mm});
            skLineSegment(sketch, "E108", {"start": v(-52.51, 63) * mm, "end": v(-58.55, 63) * mm});
            skLineSegment(sketch, "E109", {"start": v(-58.55, 63) * mm, "end": v(-60, 76.05) * mm});
            skLineSegment(sketch, "E110", {"start": v(60, -41) * mm, "end": v(59, -41) * mm});
            skLineSegment(sketch, "E111", {"start": v(-60, -41) * mm, "end": v(-59, -41) * mm});
            skSolve(sketch);
        }
        {
            var Q0;
            Q0=makeQuery(id+"F11.imprint","IMPRINT",FACE,{"disambiguationData":[TD([[makeQuery(id+"F11.imprint","IMPRINT",EDGE,{"derivedFrom":sQuery(id+"F11.wireOp",EDGE,"E80.bottom")}),-1.0]])]});
            var Q1;
            Q1=makeQuery(id+"F11.imprint","IMPRINT",FACE,{"disambiguationData":[TD([[makeQuery(id+"F11.imprint","IMPRINT",EDGE,{"derivedFrom":sQuery(id+"F11.wireOp",EDGE,"of6UWpna-Fltk-Muhk-B3aL-jeHWw9bqob6o.bottom")}),1.0]])]});
            var Q2;
            Q2=makeQuery(id+"F11.imprint","IMPRINT",FACE,{"disambiguationData":[TD([[makeQuery(id+"F11.imprint","IMPRINT",EDGE,{"derivedFrom":sQuery(id+"F11.wireOp",EDGE,"E80.left")}),-1.0]])]});
            var Q3;
            Q3=makeQuery(id+"F11.imprint","IMPRINT",FACE,{"disambiguationData":[TD([[makeQuery(id+"F11.imprint","IMPRINT",EDGE,{"derivedFrom":sQuery(id+"F11.wireOp",EDGE,"E79.bottom")}),1.0]])]});
            var Q4;
            Q4=makeQuery(id+"F11.imprint","IMPRINT",FACE,{"disambiguationData":[TD([[makeQuery(id+"F11.imprint","IMPRINT",EDGE,{"derivedFrom":sQuery(id+"F11.wireOp",EDGE,"E83.bottom")}),1.0]])]});
            var Q5;
            Q5=makeQuery(id+"F11.imprint","IMPRINT",FACE,{"disambiguationData":[TD([[makeQuery(id+"F11.imprint","IMPRINT",EDGE,{"derivedFrom":sQuery(id+"F11.wireOp",EDGE,"E83.left")}),1.0]])]});
            var Q6;
            Q6=makeQuery(id+"F11.imprint","IMPRINT",FACE,{"disambiguationData":[TD([[makeQuery(id+"F11.imprint","IMPRINT",EDGE,{"derivedFrom":sQuery(id+"F11.wireOp",EDGE,"E84.bottom")}),1.0]])]});
            var Q7;
            Q7=makeQuery(id+"F11.imprint","IMPRINT",FACE,{"disambiguationData":[TD([[makeQuery(id+"F11.imprint","IMPRINT",EDGE,{"derivedFrom":sQuery(id+"F11.wireOp",EDGE,"E84.left")}),1.0]])]});
            var Q8;
            Q8=makeQuery(id+"F11.imprint","IMPRINT",FACE,{"disambiguationData":[TD([[makeQuery(id+"F11.imprint","IMPRINT",EDGE,{"derivedFrom":sQuery(id+"F11.wireOp",EDGE,"E95.bottom")}),-1.0]])]});
            var Q9;
            Q9=makeQuery(id+"F11.imprint","IMPRINT",FACE,{"disambiguationData":[TD([[makeQuery(id+"F11.imprint","IMPRINT",EDGE,{"derivedFrom":sQuery(id+"F11.wireOp",EDGE,"E94.bottom")}),-1.0]])]});
            var Q10;
            Q10=makeQuery(id+"F11.imprint","IMPRINT",FACE,{"disambiguationData":[TD([[makeQuery(id+"F11.imprint","IMPRINT",EDGE,{"derivedFrom":sQuery(id+"F11.wireOp",EDGE,"E94.left")}),-1.0]])]});
            var Q11;
            Q11=makeQuery(id+"F11.imprint","IMPRINT",FACE,{"disambiguationData":[TD([[makeQuery(id+"F11.imprint","IMPRINT",EDGE,{"derivedFrom":sQuery(id+"F11.wireOp",EDGE,"E95.left")}),-1.0]])]});
            var Q12;
            Q12=makeQuery(id+"F11.imprint","IMPRINT",FACE,{"disambiguationData":[TD([[makeQuery(id+"F11.imprint","IMPRINT",EDGE,{"derivedFrom":sQuery(id+"F11.wireOp",EDGE,"E90.bottom")}),-1.0]])]});
            var Q13;
            Q13=makeQuery(id+"F11.imprint","IMPRINT",FACE,{"disambiguationData":[TD([[makeQuery(id+"F11.imprint","IMPRINT",EDGE,{"derivedFrom":sQuery(id+"F11.wireOp",EDGE,"E91.bottom")}),-1.0]])]});
            var Q14;
            Q14=makeQuery(id+"F11.imprint","IMPRINT",FACE,{"disambiguationData":[TD([[makeQuery(id+"F11.imprint","IMPRINT",EDGE,{"derivedFrom":sQuery(id+"F11.wireOp",EDGE,"pHr1EkMM-XxqO-or09-3az2-bhNbwgQoj8vm.bottom")}),-1.0]])]});
            var Q15;
            Q15=makeQuery(id+"F11.imprint","IMPRINT",FACE,{"disambiguationData":[TD([[makeQuery(id+"F11.imprint","IMPRINT",EDGE,{"derivedFrom":sQuery(id+"F11.wireOp",EDGE,"E91.left")}),-1.0]])]});
            var Q16;
            {var subQ0=sQuery(id+"F11.wireOp",EDGE,"E104");Q16=makeQuery(id+"F11.imprint","IMPRINT",FACE,{"disambiguationData":[TD([[makeQuery(id+"F11.imprint","IMPRINT",EDGE,{"derivedFrom":subQ0}),-1.0]])]});}
            var Q17;
            {var subQ0=sQuery(id+"F11.wireOp",EDGE,"E108");Q17=makeQuery(id+"F11.imprint","IMPRINT",FACE,{"disambiguationData":[TD([[makeQuery(id+"F11.imprint","IMPRINT",EDGE,{"derivedFrom":subQ0}),1.0]])]});}
            extrude(context, id + "F12", {"entities" : qUnion([Q0, Q1, Q2, Q3, Q4, Q5, Q6, Q7, Q8, Q9, Q10, Q11, Q12, Q13, Q14, Q15, Q16, Q17]), "oppositeDirection" : true, "depth" : 6 * mm, "offsetDistance" : 25 * mm});
        }
        {
            var Q0;
            Q0=makeQuery(id+"F12.opExtrude","SWEPT_BODY",BODY,{"disambiguationData":[OSD([sQuery(id+"F11.wireOp",EDGE,"E79.bottom"),sQuery(id+"F11.wireOp",EDGE,"E79.top"),sQuery(id+"F11.wireOp",EDGE,"E79.left"),sQuery(id+"F11.wireOp",EDGE,"E79.right")])]});
            var Q1;
            Q1=makeQuery(id+"F12.opExtrude","SWEPT_BODY",BODY,{"disambiguationData":[OSD([sQuery(id+"F11.wireOp",EDGE,"E80.bottom"),sQuery(id+"F11.wireOp",EDGE,"E80.top"),sQuery(id+"F11.wireOp",EDGE,"E80.right"),sQuery(id+"F11.wireOp",EDGE,"of6UWpna-Fltk-Muhk-B3aL-jeHWw9bqob6o.bottom"),sQuery(id+"F11.wireOp",EDGE,"of6UWpna-Fltk-Muhk-B3aL-jeHWw9bqob6o.top"),sQuery(id+"F11.wireOp",EDGE,"of6UWpna-Fltk-Muhk-B3aL-jeHWw9bqob6o.right"),sQuery(id+"F11.wireOp",EDGE,"E81"),sQuery(id+"F11.wireOp",EDGE,"bNI01JUF-0WV8-eB0Q-0p06-APX1NjNC8oJL"),sQuery(id+"F11.wireOp",EDGE,"8KMXJiwX-ChS1-D39u-T3iU-mdmO4aoYWh5v"),sQuery(id+"F11.wireOp",EDGE,"E82")])]});
            var Q2;
            Q2=makeQuery(id+"F12.opExtrude","SWEPT_BODY",BODY,{"disambiguationData":[OSD([sQuery(id+"F11.wireOp",EDGE,"E83.bottom"),sQuery(id+"F11.wireOp",EDGE,"E83.top"),sQuery(id+"F11.wireOp",EDGE,"E83.right"),sQuery(id+"F11.wireOp",EDGE,"I5T0XiVs-QQEa-CGRj-epe6-iUmXjVK8StKs"),sQuery(id+"F11.wireOp",EDGE,"E85"),sQuery(id+"F11.wireOp",EDGE,"E89"),sQuery(id+"F11.wireOp",EDGE,"VkWpw0eT-gMEt-y92e-yGvb-uSl17ukzUmqG")])]});
            var Q3;
            Q3=makeQuery(id+"F12.opExtrude","SWEPT_BODY",BODY,{"disambiguationData":[OSD([sQuery(id+"F11.wireOp",EDGE,"E84.bottom"),sQuery(id+"F11.wireOp",EDGE,"E84.top"),sQuery(id+"F11.wireOp",EDGE,"E84.right"),sQuery(id+"F11.wireOp",EDGE,"E86"),sQuery(id+"F11.wireOp",EDGE,"E87"),sQuery(id+"F11.wireOp",EDGE,"E88")])]});
            var Q4;
            Q4=makeQuery(id+"F12.opExtrude","SWEPT_BODY",BODY,{"disambiguationData":[OSD([sQuery(id+"F11.wireOp",EDGE,"E90.bottom"),sQuery(id+"F11.wireOp",EDGE,"E90.top"),sQuery(id+"F11.wireOp",EDGE,"E90.left"),sQuery(id+"F11.wireOp",EDGE,"E90.right")])]});
            var Q5;
            Q5=makeQuery(id+"F12.opExtrude","SWEPT_BODY",BODY,{"disambiguationData":[OSD([sQuery(id+"F11.wireOp",EDGE,"E95.bottom"),sQuery(id+"F11.wireOp",EDGE,"E95.top"),sQuery(id+"F11.wireOp",EDGE,"E95.right"),sQuery(id+"F11.wireOp",EDGE,"E98"),sQuery(id+"F11.wireOp",EDGE,"E99"),sQuery(id+"F11.wireOp",EDGE,"E100")])]});
            var Q6;
            Q6=makeQuery(id+"F12.opExtrude","SWEPT_BODY",BODY,{"disambiguationData":[OSD([sQuery(id+"F11.wireOp",EDGE,"E94.bottom"),sQuery(id+"F11.wireOp",EDGE,"E94.top"),sQuery(id+"F11.wireOp",EDGE,"E94.right"),sQuery(id+"F11.wireOp",EDGE,"6NTwRgHl-ybTJ-o1t6-O6oK-a0jSVvZzyGOF"),sQuery(id+"F11.wireOp",EDGE,"Hd6ebz9V-2lkx-FPWG-gXkK-h1Z5vxYtTx0a"),sQuery(id+"F11.wireOp",EDGE,"E96"),sQuery(id+"F11.wireOp",EDGE,"E97")])]});
            var Q7;
            Q7=makeQuery(id+"F12.opExtrude","SWEPT_BODY",BODY,{"disambiguationData":[OSD([sQuery(id+"F11.wireOp",EDGE,"E91.bottom"),sQuery(id+"F11.wireOp",EDGE,"E91.top"),sQuery(id+"F11.wireOp",EDGE,"E91.right"),sQuery(id+"F11.wireOp",EDGE,"pHr1EkMM-XxqO-or09-3az2-bhNbwgQoj8vm.bottom"),sQuery(id+"F11.wireOp",EDGE,"pHr1EkMM-XxqO-or09-3az2-bhNbwgQoj8vm.top"),sQuery(id+"F11.wireOp",EDGE,"pHr1EkMM-XxqO-or09-3az2-bhNbwgQoj8vm.right"),sQuery(id+"F11.wireOp",EDGE,"E92"),sQuery(id+"F11.wireOp",EDGE,"E93"),sQuery(id+"F11.wireOp",EDGE,"zz4yoj2N-bRRK-BOs6-NDRj-KNY2iRBrZ8rL"),sQuery(id+"F11.wireOp",EDGE,"axDOV24K-ICtJ-4rDI-xC8r-JKtcotBMGc8S")])]});
            var Q8;
            Q8=makeQuery(id+"F10.opExtrude","SWEPT_BODY",BODY,{"disambiguationData":[OSD([sQuery(id+"F9.wireOp",EDGE,"E76.bottom"),sQuery(id+"F9.wireOp",EDGE,"E76.top"),sQuery(id+"F9.wireOp",EDGE,"E76.left"),sQuery(id+"F9.wireOp",EDGE,"E76.right")])]});
            var Q9;
            Q9=makeQuery(id+"F10.opExtrude","SWEPT_BODY",BODY,{"disambiguationData":[OSD([sQuery(id+"F9.wireOp",EDGE,"E75.bottom"),sQuery(id+"F9.wireOp",EDGE,"E75.top"),sQuery(id+"F9.wireOp",EDGE,"E75.left"),sQuery(id+"F9.wireOp",EDGE,"E75.right")])]});
            var Q10;
            Q10=makeQuery(id+"F10.opExtrude","SWEPT_BODY",BODY,{"disambiguationData":[OSD([sQuery(id+"F0.wireOp",EDGE,"E14"),sQuery(id+"F0.wireOp",EDGE,"E33"),sQuery(id+"F9.wireOp",EDGE,"E65.bottom"),sQuery(id+"F9.wireOp",EDGE,"E65.top"),sQuery(id+"F9.wireOp",EDGE,"E65.left"),sQuery(id+"F9.wireOp",EDGE,"E65.right"),sQuery(id+"F9.wireOp",EDGE,"E70.bottom"),sQuery(id+"F9.wireOp",EDGE,"E70.top"),sQuery(id+"F9.wireOp",EDGE,"E70.right"),sQuery(id+"F9.wireOp",EDGE,"E71"),sQuery(id+"F9.wireOp",EDGE,"E72"),sQuery(id+"F9.wireOp",EDGE,"E73")])]});
            var Q11;
            Q11=makeQuery(id+"F10.opExtrude","SWEPT_BODY",BODY,{"disambiguationData":[OSD([sQuery(id+"F9.wireOp",EDGE,"E64.bottom"),sQuery(id+"F9.wireOp",EDGE,"E64.top"),sQuery(id+"F9.wireOp",EDGE,"E64.left"),sQuery(id+"F9.wireOp",EDGE,"E64.right")])]});
            var Q12;
            Q12=makeQuery(id+"F10.opExtrude","SWEPT_BODY",BODY,{"disambiguationData":[OSD([sQuery(id+"F9.wireOp",EDGE,"E62.bottom"),sQuery(id+"F9.wireOp",EDGE,"E62.top"),sQuery(id+"F9.wireOp",EDGE,"E62.left"),sQuery(id+"F9.wireOp",EDGE,"E62.right")])]});
            var Q13;
            Q13=makeQuery(id+"F10.opExtrude","SWEPT_BODY",BODY,{"disambiguationData":[OSD([sQuery(id+"F9.wireOp",EDGE,"E63.bottom"),sQuery(id+"F9.wireOp",EDGE,"E63.top"),sQuery(id+"F9.wireOp",EDGE,"E63.left"),sQuery(id+"F9.wireOp",EDGE,"E63.right")])]});
            var Q14;
            Q14=makeQuery(id+"F10.opExtrude","SWEPT_BODY",BODY,{"disambiguationData":[OSD([sQuery(id+"F0.wireOp",EDGE,"E17"),sQuery(id+"F0.wireOp",EDGE,"E34"),sQuery(id+"F9.wireOp",EDGE,"E59.bottom"),sQuery(id+"F9.wireOp",EDGE,"E59.top"),sQuery(id+"F9.wireOp",EDGE,"E59.left"),sQuery(id+"F9.wireOp",EDGE,"E59.right"),sQuery(id+"F9.wireOp",EDGE,"E60.bottom"),sQuery(id+"F9.wireOp",EDGE,"E60.top"),sQuery(id+"F9.wireOp",EDGE,"E60.right"),sQuery(id+"F9.wireOp",EDGE,"E61"),sQuery(id+"F9.wireOp",EDGE,"E68"),sQuery(id+"F9.wireOp",EDGE,"E69")])]});
            var Q15;
            Q15=makeQuery(id+"F10.opExtrude","SWEPT_BODY",BODY,{"disambiguationData":[OSD([sQuery(id+"F9.wireOp",EDGE,"E57.bottom"),sQuery(id+"F9.wireOp",EDGE,"E57.top"),sQuery(id+"F9.wireOp",EDGE,"E57.left"),sQuery(id+"F9.wireOp",EDGE,"E57.right")])]});
            var Q16;
            Q16=makeQuery(id+"F1.opExtrude","SWEPT_BODY",BODY,{"disambiguationData":[OSD([sQuery(id+"F0.wireOp",EDGE,"E0.bottom"),sQuery(id+"F0.wireOp",EDGE,"E0.left"),sQuery(id+"F0.wireOp",EDGE,"E0.right"),sQuery(id+"F0.wireOp",EDGE,"E1"),sQuery(id+"F0.wireOp",EDGE,"E2"),sQuery(id+"F0.wireOp",EDGE,"E3"),sQuery(id+"F0.wireOp",EDGE,"E4"),sQuery(id+"F0.wireOp",EDGE,"E5"),sQuery(id+"F0.wireOp",EDGE,"E6"),sQuery(id+"F0.wireOp",EDGE,"E7"),sQuery(id+"F0.wireOp",EDGE,"E8"),sQuery(id+"F0.wireOp",EDGE,"E9"),sQuery(id+"F0.wireOp",EDGE,"E10"),sQuery(id+"F0.wireOp",EDGE,"E11"),sQuery(id+"F0.wireOp",EDGE,"E12"),sQuery(id+"F0.wireOp",EDGE,"E13"),sQuery(id+"F0.wireOp",EDGE,"E14"),sQuery(id+"F0.wireOp",EDGE,"E15"),sQuery(id+"F0.wireOp",EDGE,"E16"),sQuery(id+"F0.wireOp",EDGE,"E17"),sQuery(id+"F0.wireOp",EDGE,"E20.filletArc"),sQuery(id+"F0.wireOp",EDGE,"E21.filletArc"),sQuery(id+"F0.wireOp",EDGE,"E23"),sQuery(id+"F0.wireOp",EDGE,"E24"),sQuery(id+"F0.wireOp",EDGE,"E25"),sQuery(id+"F0.wireOp",EDGE,"E26"),sQuery(id+"F0.wireOp",EDGE,"E27"),sQuery(id+"F0.wireOp",EDGE,"E28"),sQuery(id+"F0.wireOp",EDGE,"E29"),sQuery(id+"F0.wireOp",EDGE,"E30"),sQuery(id+"F0.wireOp",EDGE,"E31"),sQuery(id+"F0.wireOp",EDGE,"E32")])]});
            booleanBodies(context, id + "F13", {"operationType" : BooleanOperationType.UNION, "tools" : qUnion([Q0, Q1, Q2, Q3, Q4, Q5, Q6, Q7, Q8, Q9, Q10, Q11, Q12, Q13, Q14, Q15, Q16])});
        }
        {
            var Q0;
            Q0=makeQuery(id+"F10.opExtrude","SWEPT_FACE",FACE,{"disambiguationData":[OSD([sQuery(id+"F9.wireOp",EDGE,"E64.bottom")])]});
            var sketch = newSketch(context, id + "F14", { "sketchPlane" : qUnion([Q0])});
            skCircle(sketch, "E112", {"center": v(-63, 29) * mm, "radius": 1.25 * mm});
            skPoint(sketch, "E112.centerSnap0", {"position": v(-66, 29) * mm});
            skPoint(sketch, "E112.centerSnap1", {"position": v(-63, 32) * mm});
            skCircle(sketch, "E113", {"center": v(-63, 29) * mm, "radius": 3 * mm});
            skCircle(sketch, "E114", {"center": v(-63, 3) * mm, "radius": 1.25 * mm});
            skCircle(sketch, "E115", {"center": v(-63, 3) * mm, "radius": 3 * mm});
            skCircle(sketch, "E116", {"center": v(63, 29) * mm, "radius": 1.25 * mm});
            skCircle(sketch, "E117", {"center": v(63, 29) * mm, "radius": 3 * mm});
            skCircle(sketch, "E118", {"center": v(63, 3) * mm, "radius": 1.25 * mm});
            skCircle(sketch, "E119", {"center": v(63, 3) * mm, "radius": 3 * mm});
            skLineSegment(sketch, "E120.bottom", {"start": v(60, 32) * mm, "end": v(66, 32) * mm});
            skLineSegment(sketch, "E120.top", {"start": v(60, 26) * mm, "end": v(66, 26) * mm});
            skLineSegment(sketch, "E120.left", {"start": v(60, 32) * mm, "end": v(60, 26) * mm});
            skLineSegment(sketch, "E120.right", {"start": v(66, 32) * mm, "end": v(66, 26) * mm});
            skLineSegment(sketch, "E121.bottom", {"start": v(66, 6) * mm, "end": v(60, 6) * mm});
            skLineSegment(sketch, "E121.top", {"start": v(66, 0) * mm, "end": v(60, 0) * mm});
            skLineSegment(sketch, "E121.left", {"start": v(66, 6) * mm, "end": v(66, 0) * mm});
            skLineSegment(sketch, "E121.right", {"start": v(60, 6) * mm, "end": v(60, 0) * mm});
            skLineSegment(sketch, "E122.bottom", {"start": v(-66, 6) * mm, "end": v(-60, 6) * mm});
            skLineSegment(sketch, "E122.top", {"start": v(-66, 0) * mm, "end": v(-60, 0) * mm});
            skLineSegment(sketch, "E122.left", {"start": v(-66, 6) * mm, "end": v(-66, 0) * mm});
            skLineSegment(sketch, "E122.right", {"start": v(-60, 6) * mm, "end": v(-60, 0) * mm});
            skSolve(sketch);
        }
        {
            var Q0;
            Q0=makeQuery(id+"F13.opBoolean","MERGE",FACE,{"derivedFrom":[makeQuery(id+"F2.opExtrude","CAP_FACE",FACE,{"disambiguationData":[OSD([sQuery(id+"F0.wireOp",EDGE,"E0.left"),sQuery(id+"F0.wireOp",EDGE,"E1"),sQuery(id+"F0.wireOp",EDGE,"E6"),sQuery(id+"F0.wireOp",EDGE,"E10"),sQuery(id+"F0.wireOp",EDGE,"E20.filletArc"),sQuery(id+"F0.wireOp",EDGE,"E45"),sQuery(id+"F0.wireOp",EDGE,"E46"),sQuery(id+"F0.wireOp",EDGE,"E47.filletArc")])],"isStart":false}),makeQuery(id+"F10.opExtrude","CAP_FACE",FACE,{"disambiguationData":[OSD([sQuery(id+"F9.wireOp",EDGE,"E75.bottom"),sQuery(id+"F9.wireOp",EDGE,"E75.top"),sQuery(id+"F9.wireOp",EDGE,"E75.left"),sQuery(id+"F9.wireOp",EDGE,"E75.right")])],"isStart":true}),makeQuery(id+"F10.opExtrude","CAP_FACE",FACE,{"disambiguationData":[OSD([sQuery(id+"F9.wireOp",EDGE,"E76.bottom"),sQuery(id+"F9.wireOp",EDGE,"E76.top"),sQuery(id+"F9.wireOp",EDGE,"E76.left"),sQuery(id+"F9.wireOp",EDGE,"E76.right")])],"isStart":true})]});
            var sketch = newSketch(context, id + "F15", { "sketchPlane" : qUnion([Q0])});
            skLineSegment(sketch, "E123", {"start": v(-58, 29.4) * mm, "end": v(-50, 23.02) * mm});
            skLineSegment(sketch, "E124", {"start": v(-50, 23.02) * mm, "end": v(-42.28, 19.94) * mm});
            skLineSegment(sketch, "E125", {"start": v(-42.28, 19.94) * mm, "end": v(-31.52, 15.66) * mm});
            skLineSegment(sketch, "E126", {"start": v(-31.52, 15.66) * mm, "end": v(-30, 43) * mm});
            skLineSegment(sketch, "E127", {"start": v(-30, 43) * mm, "end": v(-53.44, 61.76) * mm});
            skSolve(sketch);
        }
        {
            var Q0;
            Q0=makeQuery(id+"F15.imprint","IMPRINT",FACE,{"disambiguationData":[TD([[makeQuery(id+"F15.imprint","IMPRINT",EDGE,{"derivedFrom":sQuery(id+"F15.wireOp",EDGE,"E123")}),1.0]])]});
            extrude(context, id + "F16", {"entities" : qUnion([Q0]), "operationType" : NewBodyOperationType.ADD, "oppositeDirection" : true, "depth" : 3 * mm, "offsetDistance" : 25 * mm});
        }
        {
            var Q0;
            Q0=makeQuery(id+"F13.opBoolean","MERGE",FACE,{"derivedFrom":[makeQuery(id+"F2.opExtrude","CAP_FACE",FACE,{"disambiguationData":[OSD([sQuery(id+"F0.wireOp",EDGE,"E0.right"),sQuery(id+"F0.wireOp",EDGE,"E3"),sQuery(id+"F0.wireOp",EDGE,"E9"),sQuery(id+"F0.wireOp",EDGE,"E11"),sQuery(id+"F0.wireOp",EDGE,"E21.filletArc"),sQuery(id+"F0.wireOp",EDGE,"E48"),sQuery(id+"F0.wireOp",EDGE,"E49"),sQuery(id+"F0.wireOp",EDGE,"E50.filletArc")])],"isStart":false}),makeQuery(id+"F10.opExtrude","CAP_FACE",FACE,{"disambiguationData":[OSD([sQuery(id+"F9.wireOp",EDGE,"E62.bottom"),sQuery(id+"F9.wireOp",EDGE,"E62.top"),sQuery(id+"F9.wireOp",EDGE,"E62.left"),sQuery(id+"F9.wireOp",EDGE,"E62.right")])],"isStart":true}),makeQuery(id+"F10.opExtrude","CAP_FACE",FACE,{"disambiguationData":[OSD([sQuery(id+"F9.wireOp",EDGE,"E63.bottom"),sQuery(id+"F9.wireOp",EDGE,"E63.top"),sQuery(id+"F9.wireOp",EDGE,"E63.left"),sQuery(id+"F9.wireOp",EDGE,"E63.right")])],"isStart":true})]});
            var sketch = newSketch(context, id + "F17", { "sketchPlane" : qUnion([Q0])});
            skLineSegment(sketch, "E128", {"start": v(53.44, 61.76) * mm, "end": v(30, 43.01) * mm});
            skLineSegment(sketch, "E129", {"start": v(30, 43.01) * mm, "end": v(31.52, 15.66) * mm});
            skLineSegment(sketch, "E130", {"start": v(31.52, 15.66) * mm, "end": v(42.29, 19.96) * mm});
            skLineSegment(sketch, "E131", {"start": v(42.29, 19.96) * mm, "end": v(50, 23) * mm});
            skLineSegment(sketch, "E132", {"start": v(50, 23) * mm, "end": v(58, 29.4) * mm});
            skSolve(sketch);
        }
        {
            var Q0;
            {var subQ12=sQuery(id+"F0.wireOp",EDGE,"E3");Q0=makeQuery(id+"F17.imprint","IMPRINT",FACE,{"disambiguationData":[TD([[makeQuery(id+"F17.imprint","IMPRINT",EDGE,{"derivedFrom":makeQuery(id+"F2.opExtrude","CAP_EDGE",EDGE,{"disambiguationData":[OSD([subQ12])],"isStart":false})}),-1.0]])]});}
            var Q1;
            Q1=makeQuery(id+"F17.imprint","IMPRINT",FACE,{"disambiguationData":[TD([[makeQuery(id+"F17.imprint","IMPRINT",EDGE,{"derivedFrom":sQuery(id+"F17.wireOp",EDGE,"E128")}),1.0]])]});
            extrude(context, id + "F18", {"entities" : qUnion([Q0, Q1]), "operationType" : NewBodyOperationType.ADD, "oppositeDirection" : true, "depth" : 3 * mm, "offsetDistance" : 25 * mm});
        }
        {
            var Q0;
            {var subQ0=sQuery(id+"F9.wireOp",EDGE,"E63.top");var subQ1=sQuery(id+"F9.wireOp",EDGE,"E63.bottom");var subQ2=sQuery(id+"F9.wireOp",EDGE,"E62.top");var subQ3=sQuery(id+"F9.wireOp",EDGE,"E62.bottom");var subQ4=sQuery(id+"F0.wireOp",EDGE,"E21.filletArc");var subQ5=sQuery(id+"F0.wireOp",EDGE,"E11");var subQ6=sQuery(id+"F0.wireOp",EDGE,"E9");var subQ7=sQuery(id+"F0.wireOp",EDGE,"E3");var subQ8=sQuery(id+"F0.wireOp",EDGE,"E0.right");var subQ9=sQuery(id+"F0.wireOp",EDGE,"E47.filletArc");var subQ10=sQuery(id+"F0.wireOp",EDGE,"E46");var subQ11=sQuery(id+"F0.wireOp",EDGE,"E45");var subQ12=sQuery(id+"F0.wireOp",EDGE,"E0.left");var subQ13=sQuery(id+"F0.wireOp",EDGE,"E33");var subQ14=sQuery(id+"F0.wireOp",EDGE,"E14");var subQ15=sQuery(id+"F0.wireOp",EDGE,"E34");var subQ16=sQuery(id+"F0.wireOp",EDGE,"E17");Q0=makeQuery(id+"F18.boolean.opBoolean","MERGE",FACE,{"derivedFrom":[makeQuery(id+"F13.opBoolean","MERGE",FACE,{"derivedFrom":[makeQuery(id+"F2.opExtrude","CAP_FACE",FACE,{"disambiguationData":[OSD([subQ8,subQ7,subQ6,subQ5,subQ4,sQuery(id+"F0.wireOp",EDGE,"E48"),sQuery(id+"F0.wireOp",EDGE,"E49"),sQuery(id+"F0.wireOp",EDGE,"E50.filletArc")])],"isStart":false}),makeQuery(id+"F10.opExtrude","CAP_FACE",FACE,{"disambiguationData":[OSD([subQ3,subQ2,sQuery(id+"F9.wireOp",EDGE,"E62.left"),sQuery(id+"F9.wireOp",EDGE,"E62.right")])],"isStart":true}),makeQuery(id+"F10.opExtrude","CAP_FACE",FACE,{"disambiguationData":[OSD([subQ1,subQ0,sQuery(id+"F9.wireOp",EDGE,"E63.left"),sQuery(id+"F9.wireOp",EDGE,"E63.right")])],"isStart":true})]}),makeQuery(id+"F16.boolean.opBoolean","MERGE",FACE,{"derivedFrom":[makeQuery(id+"F13.opBoolean","MERGE",FACE,{"derivedFrom":[makeQuery(id+"F2.opExtrude","CAP_FACE",FACE,{"disambiguationData":[OSD([sQuery(id+"F0.wireOp",EDGE,"E0.bottom"),subQ12,subQ8,sQuery(id+"F0.wireOp",EDGE,"E2"),sQuery(id+"F0.wireOp",EDGE,"E4"),sQuery(id+"F0.wireOp",EDGE,"E5"),subQ14,subQ16,subQ13,subQ15,sQuery(id+"F0.wireOp",EDGE,"E35"),sQuery(id+"F0.wireOp",EDGE,"E36"),sQuery(id+"F0.wireOp",EDGE,"E37"),sQuery(id+"F0.wireOp",EDGE,"E38"),sQuery(id+"F0.wireOp",EDGE,"E39"),sQuery(id+"F0.wireOp",EDGE,"E40"),sQuery(id+"F0.wireOp",EDGE,"E41"),sQuery(id+"F0.wireOp",EDGE,"E42")])],"isStart":false}),makeQuery(id+"F10.opExtrude","CAP_FACE",FACE,{"disambiguationData":[OSD([sQuery(id+"F9.wireOp",EDGE,"E57.bottom"),sQuery(id+"F9.wireOp",EDGE,"E57.top"),sQuery(id+"F9.wireOp",EDGE,"E57.left"),sQuery(id+"F9.wireOp",EDGE,"E57.right")])],"isStart":true}),makeQuery(id+"F10.opExtrude","CAP_FACE",FACE,{"disambiguationData":[OSD([subQ16,subQ15,sQuery(id+"F9.wireOp",EDGE,"E59.bottom"),sQuery(id+"F9.wireOp",EDGE,"E59.top"),sQuery(id+"F9.wireOp",EDGE,"E59.left"),sQuery(id+"F9.wireOp",EDGE,"E59.right"),sQuery(id+"F9.wireOp",EDGE,"E60.bottom"),sQuery(id+"F9.wireOp",EDGE,"E60.top"),sQuery(id+"F9.wireOp",EDGE,"E60.right"),sQuery(id+"F9.wireOp",EDGE,"E61"),sQuery(id+"F9.wireOp",EDGE,"E68"),sQuery(id+"F9.wireOp",EDGE,"E69")])],"isStart":true}),makeQuery(id+"F10.opExtrude","CAP_FACE",FACE,{"disambiguationData":[OSD([sQuery(id+"F9.wireOp",EDGE,"E64.bottom"),sQuery(id+"F9.wireOp",EDGE,"E64.top"),sQuery(id+"F9.wireOp",EDGE,"E64.left"),sQuery(id+"F9.wireOp",EDGE,"E64.right")])],"isStart":true}),makeQuery(id+"F10.opExtrude","CAP_FACE",FACE,{"disambiguationData":[OSD([subQ14,subQ13,sQuery(id+"F9.wireOp",EDGE,"E65.bottom"),sQuery(id+"F9.wireOp",EDGE,"E65.top"),sQuery(id+"F9.wireOp",EDGE,"E65.left"),sQuery(id+"F9.wireOp",EDGE,"E65.right"),sQuery(id+"F9.wireOp",EDGE,"E70.bottom"),sQuery(id+"F9.wireOp",EDGE,"E70.top"),sQuery(id+"F9.wireOp",EDGE,"E70.right"),sQuery(id+"F9.wireOp",EDGE,"E71"),sQuery(id+"F9.wireOp",EDGE,"E72"),sQuery(id+"F9.wireOp",EDGE,"E73")])],"isStart":true})]}),makeQuery(id+"F13.opBoolean","MERGE",FACE,{"derivedFrom":[makeQuery(id+"F2.opExtrude","CAP_FACE",FACE,{"disambiguationData":[OSD([subQ12,sQuery(id+"F0.wireOp",EDGE,"E1"),sQuery(id+"F0.wireOp",EDGE,"E6"),sQuery(id+"F0.wireOp",EDGE,"E10"),sQuery(id+"F0.wireOp",EDGE,"E20.filletArc"),subQ11,subQ10,subQ9])],"isStart":false}),makeQuery(id+"F10.opExtrude","CAP_FACE",FACE,{"disambiguationData":[OSD([sQuery(id+"F9.wireOp",EDGE,"E75.bottom"),sQuery(id+"F9.wireOp",EDGE,"E75.top"),sQuery(id+"F9.wireOp",EDGE,"E75.left"),sQuery(id+"F9.wireOp",EDGE,"E75.right")])],"isStart":true}),makeQuery(id+"F10.opExtrude","CAP_FACE",FACE,{"disambiguationData":[OSD([sQuery(id+"F9.wireOp",EDGE,"E76.bottom"),sQuery(id+"F9.wireOp",EDGE,"E76.top"),sQuery(id+"F9.wireOp",EDGE,"E76.left"),sQuery(id+"F9.wireOp",EDGE,"E76.right")])],"isStart":true})]}),makeQuery(id+"F16.opExtrude","CAP_FACE",FACE,{"disambiguationData":[OSD([subQ11,subQ10,subQ9,sQuery(id+"F15.wireOp",EDGE,"E123"),sQuery(id+"F15.wireOp",EDGE,"E124"),sQuery(id+"F15.wireOp",EDGE,"E125"),sQuery(id+"F15.wireOp",EDGE,"E126"),sQuery(id+"F15.wireOp",EDGE,"E127")])],"isStart":true})]}),makeQuery(id+"F18.opExtrude","CAP_FACE",FACE,{"disambiguationData":[OSD([subQ8,subQ7,subQ6,subQ5,subQ4,subQ3,subQ2,subQ1,subQ0,sQuery(id+"F14.wireOp",EDGE,"E117"),sQuery(id+"F14.wireOp",EDGE,"E120.bottom"),sQuery(id+"F17.wireOp",EDGE,"E128"),sQuery(id+"F17.wireOp",EDGE,"E129"),sQuery(id+"F17.wireOp",EDGE,"E130"),sQuery(id+"F17.wireOp",EDGE,"E131"),sQuery(id+"F17.wireOp",EDGE,"E132")])],"isStart":true})]});}
            var sketch = newSketch(context, id + "F19", { "sketchPlane" : qUnion([Q0])});
            skLineSegment(sketch, "E133", {"start": v(36.16, 40.26) * mm, "end": v(54, 54.52) * mm});
            skLineSegment(sketch, "E134", {"start": v(54, 54.52) * mm, "end": v(54, 33.9) * mm});
            skLineSegment(sketch, "E135", {"start": v(54, 33.9) * mm, "end": v(46.96, 28.26) * mm});
            skLineSegment(sketch, "E136", {"start": v(46.96, 28.26) * mm, "end": v(37.05, 24.34) * mm});
            skLineSegment(sketch, "E137", {"start": v(37.05, 24.34) * mm, "end": v(36.16, 40.26) * mm});
            skLineSegment(sketch, "E138", {"start": v(-36.16, 40.25) * mm, "end": v(-54, 54.52) * mm});
            skLineSegment(sketch, "E139", {"start": v(-54, 54.52) * mm, "end": v(-54, 33.9) * mm});
            skLineSegment(sketch, "E140", {"start": v(-54, 33.9) * mm, "end": v(-46.96, 28.26) * mm});
            skLineSegment(sketch, "E141", {"start": v(-46.96, 28.26) * mm, "end": v(-37.05, 24.32) * mm});
            skLineSegment(sketch, "E142", {"start": v(-37.05, 24.32) * mm, "end": v(-36.16, 40.25) * mm});
            skSolve(sketch);
        }
        {
            var Q0;
            Q0 = qSketchRegion(id + "F19", true);
            extrude(context, id + "F20", {"entities" : qUnion([Q0]), "operationType" : NewBodyOperationType.REMOVE, "oppositeDirection" : true, "depth" : 3 * mm, "offsetDistance" : 25 * mm});
        }
        {
            var Q0;
            {var subQ0=sQuery(id+"F14.wireOp",EDGE,"E122.left");var subQ1=sQuery(id+"F14.wireOp",EDGE,"E115");var subQ2=makeQuery(id+"F14.imprint","INTERSECT",VERTEX,{"derivedFrom":[subQ1,subQ0]});Q0=makeQuery(id+"F14.imprint","IMPRINT",FACE,{"disambiguationData":[TD([[makeQuery(id+"F14.imprint","IMPRINT",EDGE,{"disambiguationData":[TD([[subQ2,-1.0]])],"derivedFrom":subQ1}),-1.0]])]});}
            var Q1;
            {var subQ0=sQuery(id+"F14.wireOp",EDGE,"E122.bottom");var subQ1=sQuery(id+"F14.wireOp",EDGE,"E115");var subQ2=makeQuery(id+"F14.imprint","INTERSECT",VERTEX,{"derivedFrom":[subQ1,subQ0]});Q1=makeQuery(id+"F14.imprint","IMPRINT",FACE,{"disambiguationData":[TD([[makeQuery(id+"F14.imprint","IMPRINT",EDGE,{"disambiguationData":[TD([[subQ2,-1.0]])],"derivedFrom":subQ1}),-1.0]])]});}
            var Q2;
            Q2=makeQuery(id+"F14.imprint","IMPRINT",FACE,{"disambiguationData":[TD([[makeQuery(id+"F14.imprint","IMPRINT",EDGE,{"derivedFrom":sQuery(id+"F14.wireOp",EDGE,"E114")}),1.0]])]});
            var Q3;
            Q3=makeQuery(id+"F14.imprint","IMPRINT",FACE,{"disambiguationData":[TD([[makeQuery(id+"F14.imprint","IMPRINT",EDGE,{"derivedFrom":sQuery(id+"F14.wireOp",EDGE,"E112")}),1.0]])]});
            var Q4;
            {var subQ0=sQuery(id+"F14.wireOp",EDGE,"E113");var subQ1=sQuery(id+"F9.wireOp",EDGE,"E64.bottom");var subQ4=makeQuery(id+"F10.opExtrude","CAP_EDGE",EDGE,{"disambiguationData":[OSD([subQ1])],"isStart":false});var subQ5=makeQuery(id+"F14.imprint","INTERSECT",VERTEX,{"derivedFrom":[subQ4,subQ0]});Q4=makeQuery(id+"F14.imprint","IMPRINT",FACE,{"disambiguationData":[TD([[makeQuery(id+"F14.imprint","IMPRINT",EDGE,{"disambiguationData":[TD([[subQ5,1.0]])],"derivedFrom":subQ0}),-1.0]])]});}
            var Q5;
            {var subQ0=sQuery(id+"F14.wireOp",EDGE,"E113");var subQ1=sQuery(id+"F9.wireOp",EDGE,"E64.bottom");var subQ2=makeQuery(id+"F10.opExtrude","CAP_EDGE",EDGE,{"disambiguationData":[OSD([subQ1])],"isStart":true});var subQ3=makeQuery(id+"F14.imprint","INTERSECT",VERTEX,{"derivedFrom":[subQ2,subQ0]});Q5=makeQuery(id+"F14.imprint","IMPRINT",FACE,{"disambiguationData":[TD([[makeQuery(id+"F14.imprint","IMPRINT",EDGE,{"disambiguationData":[TD([[subQ3,-1.0]])],"derivedFrom":subQ0}),-1.0]])]});}
            var Q6;
            {var subQ0=sQuery(id+"F14.wireOp",EDGE,"E120.right");var subQ1=sQuery(id+"F14.wireOp",EDGE,"E117");var subQ2=makeQuery(id+"F14.imprint","INTERSECT",VERTEX,{"derivedFrom":[subQ1,subQ0]});Q6=makeQuery(id+"F14.imprint","IMPRINT",FACE,{"disambiguationData":[TD([[makeQuery(id+"F14.imprint","IMPRINT",EDGE,{"disambiguationData":[TD([[subQ2,1.0]])],"derivedFrom":subQ1}),-1.0]])]});}
            var Q7;
            {var subQ0=sQuery(id+"F14.wireOp",EDGE,"E120.bottom");var subQ1=sQuery(id+"F14.wireOp",EDGE,"E117");var subQ2=makeQuery(id+"F14.imprint","INTERSECT",VERTEX,{"derivedFrom":[subQ1,subQ0]});Q7=makeQuery(id+"F14.imprint","IMPRINT",FACE,{"disambiguationData":[TD([[makeQuery(id+"F14.imprint","IMPRINT",EDGE,{"disambiguationData":[TD([[subQ2,1.0]])],"derivedFrom":subQ1}),-1.0]])]});}
            var Q8;
            Q8=makeQuery(id+"F14.imprint","IMPRINT",FACE,{"disambiguationData":[TD([[makeQuery(id+"F14.imprint","IMPRINT",EDGE,{"derivedFrom":sQuery(id+"F14.wireOp",EDGE,"E116")}),1.0]])]});
            var Q9;
            {var subQ0=sQuery(id+"F14.wireOp",EDGE,"E121.bottom");var subQ1=sQuery(id+"F14.wireOp",EDGE,"E119");var subQ2=makeQuery(id+"F14.imprint","INTERSECT",VERTEX,{"derivedFrom":[subQ1,subQ0]});Q9=makeQuery(id+"F14.imprint","IMPRINT",FACE,{"disambiguationData":[TD([[makeQuery(id+"F14.imprint","IMPRINT",EDGE,{"disambiguationData":[TD([[subQ2,1.0]])],"derivedFrom":subQ1}),-1.0]])]});}
            var Q10;
            {var subQ0=sQuery(id+"F14.wireOp",EDGE,"E121.left");var subQ1=sQuery(id+"F14.wireOp",EDGE,"E119");var subQ2=makeQuery(id+"F14.imprint","INTERSECT",VERTEX,{"derivedFrom":[subQ1,subQ0]});Q10=makeQuery(id+"F14.imprint","IMPRINT",FACE,{"disambiguationData":[TD([[makeQuery(id+"F14.imprint","IMPRINT",EDGE,{"disambiguationData":[TD([[subQ2,1.0]])],"derivedFrom":subQ1}),-1.0]])]});}
            var Q11;
            Q11=makeQuery(id+"F14.imprint","IMPRINT",FACE,{"disambiguationData":[TD([[makeQuery(id+"F14.imprint","IMPRINT",EDGE,{"derivedFrom":sQuery(id+"F14.wireOp",EDGE,"E118")}),1.0]])]});
            extrude(context, id + "F21", {"entities" : qUnion([Q0, Q1, Q2, Q3, Q4, Q5, Q6, Q7, Q8, Q9, Q10, Q11]), "operationType" : NewBodyOperationType.REMOVE, "oppositeDirection" : true, "depth" : 200 * mm, "offsetDistance" : 25 * mm});
        }
        {
            var Q0;
            Q0=makeQuery(id+"F16.opExtrude","CAP_EDGE",EDGE,{"disambiguationData":[OSD([sQuery(id+"F15.wireOp",EDGE,"E125")])],"isStart":true});
            var Q1;
            Q1=makeQuery(id+"F16.opExtrude","CAP_EDGE",EDGE,{"disambiguationData":[OSD([sQuery(id+"F15.wireOp",EDGE,"E124")])],"isStart":true});
            var Q2;
            Q2=makeQuery(id+"F16.opExtrude","CAP_EDGE",EDGE,{"disambiguationData":[OSD([sQuery(id+"F15.wireOp",EDGE,"E124")])],"isStart":false});
            var Q3;
            Q3=makeQuery(id+"F16.opExtrude","CAP_EDGE",EDGE,{"disambiguationData":[OSD([sQuery(id+"F15.wireOp",EDGE,"E125")])],"isStart":false});
            var Q4;
            Q4=makeQuery(id+"F16.boolean.opBoolean","MERGE",EDGE,{"derivedFrom":[makeQuery(id+"F2.opExtrude","CAP_EDGE",EDGE,{"disambiguationData":[OSD([sQuery(id+"F0.wireOp",EDGE,"E6")])],"isStart":false}),makeQuery(id+"F16.opExtrude","CAP_EDGE",EDGE,{"disambiguationData":[OSD([sQuery(id+"F15.wireOp",EDGE,"E123")])],"isStart":true})]});
            var Q5;
            Q5=makeQuery(id+"F16.opExtrude","CAP_EDGE",EDGE,{"disambiguationData":[OSD([sQuery(id+"F15.wireOp",EDGE,"E123")])],"isStart":false});
            var Q6;
            Q6=makeQuery(id+"F20.boolean.opBoolean","COPY",EDGE,{"derivedFrom":makeQuery(id+"F20.opExtrude","CAP_EDGE",EDGE,{"disambiguationData":[OSD([sQuery(id+"F19.wireOp",EDGE,"E139")])],"isStart":true})});
            var Q7;
            Q7=makeQuery(id+"F20.boolean.opBoolean","COPY",EDGE,{"derivedFrom":makeQuery(id+"F20.opExtrude","CAP_EDGE",EDGE,{"disambiguationData":[OSD([sQuery(id+"F19.wireOp",EDGE,"E138")])],"isStart":true})});
            var Q8;
            Q8=makeQuery(id+"F20.boolean.opBoolean","COPY",EDGE,{"derivedFrom":makeQuery(id+"F20.opExtrude","CAP_EDGE",EDGE,{"disambiguationData":[OSD([sQuery(id+"F19.wireOp",EDGE,"E142")])],"isStart":true})});
            var Q9;
            Q9=makeQuery(id+"F20.boolean.opBoolean","COPY",EDGE,{"derivedFrom":makeQuery(id+"F20.opExtrude","CAP_EDGE",EDGE,{"disambiguationData":[OSD([sQuery(id+"F19.wireOp",EDGE,"E141")])],"isStart":true})});
            var Q10;
            Q10=makeQuery(id+"F20.boolean.opBoolean","COPY",EDGE,{"derivedFrom":makeQuery(id+"F20.opExtrude","CAP_EDGE",EDGE,{"disambiguationData":[OSD([sQuery(id+"F19.wireOp",EDGE,"E140")])],"isStart":true})});
            var Q11;
            Q11=makeQuery(id+"F20.boolean.opBoolean","INTERSECT",EDGE,{"derivedFrom":[makeQuery(id+"F16.opExtrude","CAP_FACE",FACE,{"disambiguationData":[OSD([sQuery(id+"F0.wireOp",EDGE,"E45"),sQuery(id+"F0.wireOp",EDGE,"E46"),sQuery(id+"F0.wireOp",EDGE,"E47.filletArc"),sQuery(id+"F15.wireOp",EDGE,"E123"),sQuery(id+"F15.wireOp",EDGE,"E124"),sQuery(id+"F15.wireOp",EDGE,"E125"),sQuery(id+"F15.wireOp",EDGE,"E126"),sQuery(id+"F15.wireOp",EDGE,"E127")])],"isStart":false}),makeQuery(id+"F20.opExtrude","SWEPT_FACE",FACE,{"disambiguationData":[OSD([sQuery(id+"F19.wireOp",EDGE,"E140")])]})]});
            var Q12;
            Q12=makeQuery(id+"F20.boolean.opBoolean","INTERSECT",EDGE,{"derivedFrom":[makeQuery(id+"F16.opExtrude","CAP_FACE",FACE,{"disambiguationData":[OSD([sQuery(id+"F0.wireOp",EDGE,"E45"),sQuery(id+"F0.wireOp",EDGE,"E46"),sQuery(id+"F0.wireOp",EDGE,"E47.filletArc"),sQuery(id+"F15.wireOp",EDGE,"E123"),sQuery(id+"F15.wireOp",EDGE,"E124"),sQuery(id+"F15.wireOp",EDGE,"E125"),sQuery(id+"F15.wireOp",EDGE,"E126"),sQuery(id+"F15.wireOp",EDGE,"E127")])],"isStart":false}),makeQuery(id+"F20.opExtrude","SWEPT_FACE",FACE,{"disambiguationData":[OSD([sQuery(id+"F19.wireOp",EDGE,"E141")])]})]});
            var Q13;
            Q13=makeQuery(id+"F20.boolean.opBoolean","INTERSECT",EDGE,{"derivedFrom":[makeQuery(id+"F16.opExtrude","CAP_FACE",FACE,{"disambiguationData":[OSD([sQuery(id+"F0.wireOp",EDGE,"E45"),sQuery(id+"F0.wireOp",EDGE,"E46"),sQuery(id+"F0.wireOp",EDGE,"E47.filletArc"),sQuery(id+"F15.wireOp",EDGE,"E123"),sQuery(id+"F15.wireOp",EDGE,"E124"),sQuery(id+"F15.wireOp",EDGE,"E125"),sQuery(id+"F15.wireOp",EDGE,"E126"),sQuery(id+"F15.wireOp",EDGE,"E127")])],"isStart":false}),makeQuery(id+"F20.opExtrude","SWEPT_FACE",FACE,{"disambiguationData":[OSD([sQuery(id+"F19.wireOp",EDGE,"E139")])]})]});
            var Q14;
            Q14=makeQuery(id+"F20.boolean.opBoolean","INTERSECT",EDGE,{"derivedFrom":[makeQuery(id+"F16.opExtrude","CAP_FACE",FACE,{"disambiguationData":[OSD([sQuery(id+"F0.wireOp",EDGE,"E45"),sQuery(id+"F0.wireOp",EDGE,"E46"),sQuery(id+"F0.wireOp",EDGE,"E47.filletArc"),sQuery(id+"F15.wireOp",EDGE,"E123"),sQuery(id+"F15.wireOp",EDGE,"E124"),sQuery(id+"F15.wireOp",EDGE,"E125"),sQuery(id+"F15.wireOp",EDGE,"E126"),sQuery(id+"F15.wireOp",EDGE,"E127")])],"isStart":false}),makeQuery(id+"F20.opExtrude","SWEPT_FACE",FACE,{"disambiguationData":[OSD([sQuery(id+"F19.wireOp",EDGE,"E138")])]})]});
            var Q15;
            Q15=makeQuery(id+"F20.boolean.opBoolean","INTERSECT",EDGE,{"derivedFrom":[makeQuery(id+"F16.opExtrude","CAP_FACE",FACE,{"disambiguationData":[OSD([sQuery(id+"F0.wireOp",EDGE,"E45"),sQuery(id+"F0.wireOp",EDGE,"E46"),sQuery(id+"F0.wireOp",EDGE,"E47.filletArc"),sQuery(id+"F15.wireOp",EDGE,"E123"),sQuery(id+"F15.wireOp",EDGE,"E124"),sQuery(id+"F15.wireOp",EDGE,"E125"),sQuery(id+"F15.wireOp",EDGE,"E126"),sQuery(id+"F15.wireOp",EDGE,"E127")])],"isStart":false}),makeQuery(id+"F20.opExtrude","SWEPT_FACE",FACE,{"disambiguationData":[OSD([sQuery(id+"F19.wireOp",EDGE,"E142")])]})]});
            var Q16;
            Q16=makeQuery(id+"F16.opExtrude","CAP_EDGE",EDGE,{"disambiguationData":[OSD([sQuery(id+"F15.wireOp",EDGE,"E127")])],"isStart":true});
            var Q17;
            Q17=makeQuery(id+"F20.boolean.opBoolean","COPY",EDGE,{"derivedFrom":makeQuery(id+"F20.opExtrude","CAP_EDGE",EDGE,{"disambiguationData":[OSD([sQuery(id+"F19.wireOp",EDGE,"E136")])],"isStart":true})});
            var Q18;
            Q18=makeQuery(id+"F20.boolean.opBoolean","COPY",EDGE,{"derivedFrom":makeQuery(id+"F20.opExtrude","CAP_EDGE",EDGE,{"disambiguationData":[OSD([sQuery(id+"F19.wireOp",EDGE,"E136")])],"isStart":false})});
            var Q19;
            Q19=makeQuery(id+"F20.boolean.opBoolean","COPY",EDGE,{"derivedFrom":makeQuery(id+"F20.opExtrude","CAP_EDGE",EDGE,{"disambiguationData":[OSD([sQuery(id+"F19.wireOp",EDGE,"E137")])],"isStart":true})});
            var Q20;
            Q20=makeQuery(id+"F20.boolean.opBoolean","COPY",EDGE,{"derivedFrom":makeQuery(id+"F20.opExtrude","CAP_EDGE",EDGE,{"disambiguationData":[OSD([sQuery(id+"F19.wireOp",EDGE,"E137")])],"isStart":false})});
            var Q21;
            Q21=makeQuery(id+"F20.boolean.opBoolean","COPY",EDGE,{"derivedFrom":makeQuery(id+"F20.opExtrude","CAP_EDGE",EDGE,{"disambiguationData":[OSD([sQuery(id+"F19.wireOp",EDGE,"E135")])],"isStart":false})});
            var Q22;
            Q22=makeQuery(id+"F20.boolean.opBoolean","COPY",EDGE,{"derivedFrom":makeQuery(id+"F20.opExtrude","CAP_EDGE",EDGE,{"disambiguationData":[OSD([sQuery(id+"F19.wireOp",EDGE,"E134")])],"isStart":true})});
            var Q23;
            Q23=makeQuery(id+"F20.boolean.opBoolean","COPY",EDGE,{"derivedFrom":makeQuery(id+"F20.opExtrude","CAP_EDGE",EDGE,{"disambiguationData":[OSD([sQuery(id+"F19.wireOp",EDGE,"E133")])],"isStart":true})});
            var Q24;
            Q24=makeQuery(id+"F18.opExtrude","CAP_EDGE",EDGE,{"disambiguationData":[OSD([sQuery(id+"F17.wireOp",EDGE,"E128")])],"isStart":true});
            var Q25;
            Q25=makeQuery(id+"F18.opExtrude","CAP_EDGE",EDGE,{"disambiguationData":[OSD([sQuery(id+"F17.wireOp",EDGE,"E128")])],"isStart":false});
            var Q26;
            Q26=makeQuery(id+"F2.opExtrude","CAP_EDGE",EDGE,{"disambiguationData":[OSD([sQuery(id+"F0.wireOp",EDGE,"E21.filletArc")])],"isStart":false});
            var Q27;
            Q27=makeQuery(id+"F18.opExtrude","CAP_EDGE",EDGE,{"disambiguationData":[OSD([sQuery(id+"F17.wireOp",EDGE,"E132")])],"isStart":true});
            var Q28;
            Q28=makeQuery(id+"F18.opExtrude","CAP_EDGE",EDGE,{"disambiguationData":[OSD([sQuery(id+"F17.wireOp",EDGE,"E131")])],"isStart":true});
            var Q29;
            Q29=makeQuery(id+"F18.opExtrude","CAP_EDGE",EDGE,{"disambiguationData":[OSD([sQuery(id+"F17.wireOp",EDGE,"E130")])],"isStart":true});
            var Q30;
            Q30=makeQuery(id+"F18.opExtrude","CAP_EDGE",EDGE,{"disambiguationData":[OSD([sQuery(id+"F17.wireOp",EDGE,"E132")])],"isStart":false});
            var Q31;
            Q31=makeQuery(id+"F18.opExtrude","CAP_EDGE",EDGE,{"disambiguationData":[OSD([sQuery(id+"F17.wireOp",EDGE,"E131")])],"isStart":false});
            var Q32;
            Q32=makeQuery(id+"F18.opExtrude","CAP_EDGE",EDGE,{"disambiguationData":[OSD([sQuery(id+"F17.wireOp",EDGE,"E130")])],"isStart":false});
            var Q33;
            Q33=makeQuery(id+"F2.opExtrude","CAP_EDGE",EDGE,{"disambiguationData":[OSD([sQuery(id+"F0.wireOp",EDGE,"E20.filletArc")])],"isStart":false});
            var Q34;
            Q34=makeQuery(id+"F16.opExtrude","CAP_EDGE",EDGE,{"disambiguationData":[OSD([sQuery(id+"F15.wireOp",EDGE,"E127")])],"isStart":false});
            var Q35;
            Q35=makeQuery(id+"F1.opExtrude","CAP_EDGE",EDGE,{"disambiguationData":[OSD([sQuery(id+"F0.wireOp",EDGE,"E1")])],"isStart":true});
            var Q36;
            Q36=makeQuery(id+"F1.opExtrude","CAP_EDGE",EDGE,{"disambiguationData":[OSD([sQuery(id+"F0.wireOp",EDGE,"E16")])],"isStart":true});
            var Q37;
            Q37=makeQuery(id+"F1.opExtrude","CAP_EDGE",EDGE,{"disambiguationData":[OSD([sQuery(id+"F0.wireOp",EDGE,"E2")])],"isStart":true});
            fillet(context, id + "F22", {"entities" : qUnion([Q0, Q1, Q2, Q3, Q4, Q5, Q6, Q7, Q8, Q9, Q10, Q11, Q12, Q13, Q14, Q15, Q16, Q17, Q18, Q19, Q20, Q21, Q22, Q23, Q24, Q25, Q26, Q27, Q28, Q29, Q30, Q31, Q32, Q33, Q34, Q35, Q36, Q37]), "radius" : 1 * mm, "tangentPropagation" : true, "allowEdgeOverflow" : false});
        }
        {
            var Q0;
            {var subQ0=sQuery(id+"F0.wireOp",EDGE,"E0.left");var subQ1=makeQuery(id+"F0.imprint","IMPRINT",EDGE,{"disambiguationData":[TD([[makeQuery(id+"F0.imprint","INTERSECT",VERTEX,{"derivedFrom":[subQ0,sQuery(id+"F0.wireOp",EDGE,"E20.filletArc")]}),1.0]])],"derivedFrom":subQ0});Q0=makeQuery(id+"F2.boolean.opBoolean","MERGE",FACE,{"derivedFrom":[makeQuery(id+"F1.opExtrude","SWEPT_FACE",FACE,{"disambiguationData":[OSD([subQ0]),TDD([subQ1])]}),makeQuery(id+"F2.opExtrude","SWEPT_FACE",FACE,{"disambiguationData":[OSD([subQ0]),TDD([subQ1])]})]});}
            var sketch = newSketch(context, id + "F23", { "sketchPlane" : qUnion([Q0])});
            skLineSegment(sketch, "E143.bottom", {"start": v(-53, 9) * mm, "end": v(-41, 9) * mm});
            skLineSegment(sketch, "E143.top", {"start": v(-53, 23) * mm, "end": v(-41, 23) * mm});
            skLineSegment(sketch, "E143.left", {"start": v(-56, 12) * mm, "end": v(-56, 20) * mm});
            skLineSegment(sketch, "E143.right", {"start": v(-38, 12) * mm, "end": v(-38, 20) * mm});
            skPoint(sketch, "E144.visualSharp", {"position": v(-56, 23) * mm});
            skArc(sketch, "E144.filletArc", {"start": v(-53, 23) * mm, "mid": v(-55.13, 22.12) * mm, "end": v(-56, 20) * mm});
            skPoint(sketch, "E145.visualSharp", {"position": v(-56, 9) * mm});
            skArc(sketch, "E145.filletArc", {"start": v(-56, 12) * mm, "mid": v(-55.13, 9.88) * mm, "end": v(-53, 9) * mm});
            skPoint(sketch, "E146.visualSharp", {"position": v(-38, 9) * mm});
            skArc(sketch, "E146.filletArc", {"start": v(-41, 9) * mm, "mid": v(-38.89, 9.88) * mm, "end": v(-38, 12) * mm});
            skPoint(sketch, "E147.visualSharp", {"position": v(-38, 23) * mm});
            skArc(sketch, "E147.filletArc", {"start": v(-38, 20) * mm, "mid": v(-38.89, 22.12) * mm, "end": v(-41, 23) * mm});
            skSolve(sketch);
        }
        {
            var Q0;
            Q0=makeQuery(id+"F23.imprint","IMPRINT",FACE,{"disambiguationData":[TD([[makeQuery(id+"F23.imprint","IMPRINT",EDGE,{"derivedFrom":sQuery(id+"F23.wireOp",EDGE,"E143.bottom")}),1.0]])]});
            extrude(context, id + "F24", {"entities" : qUnion([Q0]), "operationType" : NewBodyOperationType.REMOVE, "oppositeDirection" : true, "depth" : 5 * mm, "offsetDistance" : 25 * mm});
        }
        {
            var Q0;
            {var subQ0=sQuery(id+"F0.wireOp",EDGE,"E0.right");var subQ1=makeQuery(id+"F0.imprint","IMPRINT",EDGE,{"disambiguationData":[TD([[makeQuery(id+"F0.imprint","INTERSECT",VERTEX,{"derivedFrom":[subQ0,sQuery(id+"F0.wireOp",EDGE,"E21.filletArc")]}),1.0]])],"derivedFrom":subQ0});Q0=makeQuery(id+"F2.boolean.opBoolean","MERGE",FACE,{"derivedFrom":[makeQuery(id+"F1.opExtrude","SWEPT_FACE",FACE,{"disambiguationData":[OSD([subQ0]),TDD([subQ1])]}),makeQuery(id+"F2.opExtrude","SWEPT_FACE",FACE,{"disambiguationData":[OSD([subQ0]),TDD([subQ1])]})]});}
            var sketch = newSketch(context, id + "F25", { "sketchPlane" : qUnion([Q0])});
            skLineSegment(sketch, "E148.bottom", {"start": v(41, 9) * mm, "end": v(53, 9) * mm});
            skLineSegment(sketch, "E148.top", {"start": v(41, 23) * mm, "end": v(53, 23) * mm});
            skLineSegment(sketch, "E148.left", {"start": v(38, 12) * mm, "end": v(38, 20) * mm});
            skLineSegment(sketch, "E148.right", {"start": v(56, 12) * mm, "end": v(56, 20) * mm});
            skPoint(sketch, "E149.visualSharp", {"position": v(38, 23) * mm});
            skArc(sketch, "E149.filletArc", {"start": v(41, 23) * mm, "mid": v(38.89, 22.12) * mm, "end": v(38, 20) * mm});
            skPoint(sketch, "E150.visualSharp", {"position": v(38, 9) * mm});
            skArc(sketch, "E150.filletArc", {"start": v(38, 12) * mm, "mid": v(38.89, 9.88) * mm, "end": v(41, 9) * mm});
            skPoint(sketch, "E151.visualSharp", {"position": v(56, 9) * mm});
            skArc(sketch, "E151.filletArc", {"start": v(53, 9) * mm, "mid": v(55.13, 9.88) * mm, "end": v(56, 12) * mm});
            skPoint(sketch, "E152.visualSharp", {"position": v(56, 23) * mm});
            skArc(sketch, "E152.filletArc", {"start": v(56, 20) * mm, "mid": v(55.13, 22.12) * mm, "end": v(53, 23) * mm});
            skSolve(sketch);
        }
        {
            var Q0;
            Q0=makeQuery(id+"F25.imprint","IMPRINT",FACE,{"disambiguationData":[TD([[makeQuery(id+"F25.imprint","IMPRINT",EDGE,{"derivedFrom":sQuery(id+"F25.wireOp",EDGE,"E148.bottom")}),1.0]])]});
            extrude(context, id + "F26", {"entities" : qUnion([Q0]), "operationType" : NewBodyOperationType.REMOVE, "oppositeDirection" : true, "depth" : 4 * mm, "offsetDistance" : 25 * mm});
        }
        {
            var Q0;
            {var subQ0=sQuery(id+"F9.wireOp",EDGE,"E63.right");var subQ1=sQuery(id+"F9.wireOp",EDGE,"E63.top");var subQ2=sQuery(id+"F9.wireOp",EDGE,"E63.bottom");var subQ3=sQuery(id+"F9.wireOp",EDGE,"E62.right");var subQ4=sQuery(id+"F9.wireOp",EDGE,"E62.top");var subQ5=sQuery(id+"F9.wireOp",EDGE,"E62.bottom");var subQ6=sQuery(id+"F0.wireOp",EDGE,"E21.filletArc");var subQ7=sQuery(id+"F0.wireOp",EDGE,"E11");var subQ8=sQuery(id+"F0.wireOp",EDGE,"E9");var subQ9=sQuery(id+"F0.wireOp",EDGE,"E3");var subQ10=sQuery(id+"F0.wireOp",EDGE,"E0.right");var subQ11=sQuery(id+"F0.wireOp",EDGE,"E47.filletArc");var subQ12=sQuery(id+"F0.wireOp",EDGE,"E46");var subQ13=sQuery(id+"F0.wireOp",EDGE,"E45");var subQ14=sQuery(id+"F0.wireOp",EDGE,"E0.left");var subQ15=sQuery(id+"F0.wireOp",EDGE,"E33");var subQ16=sQuery(id+"F0.wireOp",EDGE,"E14");var subQ17=sQuery(id+"F0.wireOp",EDGE,"E34");var subQ18=sQuery(id+"F0.wireOp",EDGE,"E17");Q0=makeQuery(id+"F18.boolean.opBoolean","MERGE",FACE,{"derivedFrom":[makeQuery(id+"F13.opBoolean","MERGE",FACE,{"derivedFrom":[makeQuery(id+"F2.opExtrude","CAP_FACE",FACE,{"disambiguationData":[OSD([subQ10,subQ9,subQ8,subQ7,subQ6,sQuery(id+"F0.wireOp",EDGE,"E48"),sQuery(id+"F0.wireOp",EDGE,"E49"),sQuery(id+"F0.wireOp",EDGE,"E50.filletArc")])],"isStart":false}),makeQuery(id+"F10.opExtrude","CAP_FACE",FACE,{"disambiguationData":[OSD([subQ5,subQ4,sQuery(id+"F9.wireOp",EDGE,"E62.left"),subQ3])],"isStart":true}),makeQuery(id+"F10.opExtrude","CAP_FACE",FACE,{"disambiguationData":[OSD([subQ2,subQ1,sQuery(id+"F9.wireOp",EDGE,"E63.left"),subQ0])],"isStart":true})]}),makeQuery(id+"F16.boolean.opBoolean","MERGE",FACE,{"derivedFrom":[makeQuery(id+"F13.opBoolean","MERGE",FACE,{"derivedFrom":[makeQuery(id+"F2.opExtrude","CAP_FACE",FACE,{"disambiguationData":[OSD([sQuery(id+"F0.wireOp",EDGE,"E0.bottom"),subQ14,subQ10,sQuery(id+"F0.wireOp",EDGE,"E2"),sQuery(id+"F0.wireOp",EDGE,"E4"),sQuery(id+"F0.wireOp",EDGE,"E5"),subQ16,subQ18,subQ15,subQ17,sQuery(id+"F0.wireOp",EDGE,"E35"),sQuery(id+"F0.wireOp",EDGE,"E36"),sQuery(id+"F0.wireOp",EDGE,"E37"),sQuery(id+"F0.wireOp",EDGE,"E38"),sQuery(id+"F0.wireOp",EDGE,"E39"),sQuery(id+"F0.wireOp",EDGE,"E40"),sQuery(id+"F0.wireOp",EDGE,"E41"),sQuery(id+"F0.wireOp",EDGE,"E42")])],"isStart":false}),makeQuery(id+"F10.opExtrude","CAP_FACE",FACE,{"disambiguationData":[OSD([sQuery(id+"F9.wireOp",EDGE,"E57.bottom"),sQuery(id+"F9.wireOp",EDGE,"E57.top"),sQuery(id+"F9.wireOp",EDGE,"E57.left"),sQuery(id+"F9.wireOp",EDGE,"E57.right")])],"isStart":true}),makeQuery(id+"F10.opExtrude","CAP_FACE",FACE,{"disambiguationData":[OSD([subQ18,subQ17,sQuery(id+"F9.wireOp",EDGE,"E59.bottom"),sQuery(id+"F9.wireOp",EDGE,"E59.top"),sQuery(id+"F9.wireOp",EDGE,"E59.left"),sQuery(id+"F9.wireOp",EDGE,"E59.right"),sQuery(id+"F9.wireOp",EDGE,"E60.bottom"),sQuery(id+"F9.wireOp",EDGE,"E60.top"),sQuery(id+"F9.wireOp",EDGE,"E60.right"),sQuery(id+"F9.wireOp",EDGE,"E61"),sQuery(id+"F9.wireOp",EDGE,"E68"),sQuery(id+"F9.wireOp",EDGE,"E69")])],"isStart":true}),makeQuery(id+"F10.opExtrude","CAP_FACE",FACE,{"disambiguationData":[OSD([sQuery(id+"F9.wireOp",EDGE,"E64.bottom"),sQuery(id+"F9.wireOp",EDGE,"E64.top"),sQuery(id+"F9.wireOp",EDGE,"E64.left"),sQuery(id+"F9.wireOp",EDGE,"E64.right")])],"isStart":true}),makeQuery(id+"F10.opExtrude","CAP_FACE",FACE,{"disambiguationData":[OSD([subQ16,subQ15,sQuery(id+"F9.wireOp",EDGE,"E65.bottom"),sQuery(id+"F9.wireOp",EDGE,"E65.top"),sQuery(id+"F9.wireOp",EDGE,"E65.left"),sQuery(id+"F9.wireOp",EDGE,"E65.right"),sQuery(id+"F9.wireOp",EDGE,"E70.bottom"),sQuery(id+"F9.wireOp",EDGE,"E70.top"),sQuery(id+"F9.wireOp",EDGE,"E70.right"),sQuery(id+"F9.wireOp",EDGE,"E71"),sQuery(id+"F9.wireOp",EDGE,"E72"),sQuery(id+"F9.wireOp",EDGE,"E73")])],"isStart":true})]}),makeQuery(id+"F13.opBoolean","MERGE",FACE,{"derivedFrom":[makeQuery(id+"F2.opExtrude","CAP_FACE",FACE,{"disambiguationData":[OSD([subQ14,sQuery(id+"F0.wireOp",EDGE,"E1"),sQuery(id+"F0.wireOp",EDGE,"E6"),sQuery(id+"F0.wireOp",EDGE,"E10"),sQuery(id+"F0.wireOp",EDGE,"E20.filletArc"),subQ13,subQ12,subQ11])],"isStart":false}),makeQuery(id+"F10.opExtrude","CAP_FACE",FACE,{"disambiguationData":[OSD([sQuery(id+"F9.wireOp",EDGE,"E75.bottom"),sQuery(id+"F9.wireOp",EDGE,"E75.top"),sQuery(id+"F9.wireOp",EDGE,"E75.left"),sQuery(id+"F9.wireOp",EDGE,"E75.right")])],"isStart":true}),makeQuery(id+"F10.opExtrude","CAP_FACE",FACE,{"disambiguationData":[OSD([sQuery(id+"F9.wireOp",EDGE,"E76.bottom"),sQuery(id+"F9.wireOp",EDGE,"E76.top"),sQuery(id+"F9.wireOp",EDGE,"E76.left"),sQuery(id+"F9.wireOp",EDGE,"E76.right")])],"isStart":true})]}),makeQuery(id+"F16.opExtrude","CAP_FACE",FACE,{"disambiguationData":[OSD([subQ13,subQ12,subQ11,sQuery(id+"F15.wireOp",EDGE,"E123"),sQuery(id+"F15.wireOp",EDGE,"E124"),sQuery(id+"F15.wireOp",EDGE,"E125"),sQuery(id+"F15.wireOp",EDGE,"E126"),sQuery(id+"F15.wireOp",EDGE,"E127")])],"isStart":true})]}),makeQuery(id+"F18.opExtrude","CAP_FACE",FACE,{"disambiguationData":[OSD([subQ10,subQ9,subQ8,subQ7,subQ6,subQ5,subQ4,subQ3,subQ2,subQ1,subQ0,sQuery(id+"F17.wireOp",EDGE,"E128"),sQuery(id+"F17.wireOp",EDGE,"E129"),sQuery(id+"F17.wireOp",EDGE,"E130"),sQuery(id+"F17.wireOp",EDGE,"E131"),sQuery(id+"F17.wireOp",EDGE,"E132")])],"isStart":true})]});}
            var sketch = newSketch(context, id + "F27", { "sketchPlane" : qUnion([Q0])});
            skLineSegment(sketch, "E153", {"start": v(34.67, -41) * mm, "end": v(40.67, -41) * mm});
            skLineSegment(sketch, "E154", {"start": v(40.67, -41) * mm, "end": v(40.67, -51.86) * mm});
            skLineSegment(sketch, "E155", {"start": v(34.33, -35) * mm, "end": v(40.67, -35) * mm});
            skLineSegment(sketch, "E156", {"start": v(40.67, -35) * mm, "end": v(40.67, -29) * mm});
            skLineSegment(sketch, "E157", {"start": v(40.67, -29) * mm, "end": v(34, -29) * mm});
            skLineSegment(sketch, "E158", {"start": v(-34.67, -41) * mm, "end": v(-40.67, -41) * mm});
            skLineSegment(sketch, "E159", {"start": v(-40.67, -41) * mm, "end": v(-40.67, -51.86) * mm});
            skLineSegment(sketch, "E160", {"start": v(-34, -29) * mm, "end": v(-40.67, -29) * mm});
            skLineSegment(sketch, "E161", {"start": v(-40.67, -29) * mm, "end": v(-40.67, -35) * mm});
            skLineSegment(sketch, "E162", {"start": v(-40.67, -35) * mm, "end": v(-34.33, -35) * mm});
            skSolve(sketch);
        }
        {
            var Q0;
            {var subQ0=sQuery(id+"F27.wireOp",EDGE,"E155");Q0=makeQuery(id+"F27.imprint","IMPRINT",FACE,{"disambiguationData":[TD([[makeQuery(id+"F27.imprint","IMPRINT",EDGE,{"derivedFrom":subQ0}),1.0]])]});}
            var Q1;
            {var subQ0=sQuery(id+"F27.wireOp",EDGE,"E153");Q1=makeQuery(id+"F27.imprint","IMPRINT",FACE,{"disambiguationData":[TD([[makeQuery(id+"F27.imprint","IMPRINT",EDGE,{"derivedFrom":subQ0}),-1.0]])]});}
            var Q2;
            {var subQ0=sQuery(id+"F27.wireOp",EDGE,"E158");Q2=makeQuery(id+"F27.imprint","IMPRINT",FACE,{"disambiguationData":[TD([[makeQuery(id+"F27.imprint","IMPRINT",EDGE,{"derivedFrom":subQ0}),1.0]])]});}
            var Q3;
            {var subQ0=sQuery(id+"F27.wireOp",EDGE,"E160");Q3=makeQuery(id+"F27.imprint","IMPRINT",FACE,{"disambiguationData":[TD([[makeQuery(id+"F27.imprint","IMPRINT",EDGE,{"derivedFrom":subQ0}),1.0]])]});}
            extrude(context, id + "F28", {"entities" : qUnion([Q0, Q1, Q2, Q3]), "operationType" : NewBodyOperationType.ADD, "oppositeDirection" : true, "depth" : 6 * mm, "offsetDistance" : 25 * mm});
        }
        {
            var Q0;
            Q0=makeQuery(id+"F28.opExtrude","SWEPT_FACE",FACE,{"disambiguationData":[OSD([sQuery(id+"F27.wireOp",EDGE,"E157")])]});
            var sketch = newSketch(context, id + "F29", { "sketchPlane" : qUnion([Q0])});
            skPoint(sketch, "E163.centerSnap0", {"position": v(-40.67, 29) * mm});
            skCircle(sketch, "E164", {"center": v(-37.67, 29) * mm, "radius": 1.25 * mm});
            skCircle(sketch, "E165", {"center": v(37.67, 29) * mm, "radius": 1.25 * mm});
            skSolve(sketch);
        }
        {
            var Q0;
            Q0=makeQuery(id+"F29.imprint","IMPRINT",FACE,{"disambiguationData":[TD([[makeQuery(id+"F29.imprint","IMPRINT",EDGE,{"derivedFrom":sQuery(id+"F29.wireOp",EDGE,"E164")}),1.0]])]});
            var Q1;
            Q1=makeQuery(id+"F29.imprint","IMPRINT",FACE,{"disambiguationData":[TD([[makeQuery(id+"F29.imprint","IMPRINT",EDGE,{"derivedFrom":sQuery(id+"F29.wireOp",EDGE,"E165")}),1.0]])]});
            extrude(context, id + "F30", {"entities" : qUnion([Q0, Q1]), "operationType" : NewBodyOperationType.REMOVE, "oppositeDirection" : true, "depth" : 25 * mm, "offsetDistance" : 25 * mm});
        }
        {
            var Q0;
            Q0=makeQuery(id+"F28.opExtrude","CAP_EDGE",EDGE,{"disambiguationData":[OSD([sQuery(id+"F27.wireOp",EDGE,"E156")])],"isStart":true});
            var Q1;
            Q1=makeQuery(id+"F28.opExtrude","CAP_EDGE",EDGE,{"disambiguationData":[OSD([sQuery(id+"F27.wireOp",EDGE,"E156")])],"isStart":false});
            var Q2;
            Q2=makeQuery(id+"F28.opExtrude","CAP_EDGE",EDGE,{"disambiguationData":[OSD([sQuery(id+"F27.wireOp",EDGE,"E154")])],"isStart":true});
            var Q3;
            {var subQ0=sQuery(id+"F27.wireOp",EDGE,"E154");Q3=makeQuery(id+"F28.boolean.opBoolean","SPLIT",EDGE,{"disambiguationData":[topologyDisambiguationEdgeConnected([makeQuery(id+"F28.opExtrude","CAP_FACE",FACE,{"disambiguationData":[OSD([sQuery(id+"F0.wireOp",EDGE,"E5"),sQuery(id+"F0.wireOp",EDGE,"E17"),sQuery(id+"F27.wireOp",EDGE,"E153"),subQ0])],"isStart":false})])],"derivedFrom":makeQuery(id+"F28.opExtrude","CAP_EDGE",EDGE,{"disambiguationData":[OSD([subQ0])],"isStart":false})});}
            var Q4;
            Q4=makeQuery(id+"F28.opExtrude","CAP_EDGE",EDGE,{"disambiguationData":[OSD([sQuery(id+"F27.wireOp",EDGE,"E159")])],"isStart":true});
            var Q5;
            Q5=makeQuery(id+"F28.opExtrude","CAP_EDGE",EDGE,{"disambiguationData":[OSD([sQuery(id+"F27.wireOp",EDGE,"E159")])],"isStart":false});
            var Q6;
            Q6=makeQuery(id+"F28.opExtrude","CAP_EDGE",EDGE,{"disambiguationData":[OSD([sQuery(id+"F27.wireOp",EDGE,"E161")])],"isStart":true});
            var Q7;
            Q7=makeQuery(id+"F28.opExtrude","CAP_EDGE",EDGE,{"disambiguationData":[OSD([sQuery(id+"F27.wireOp",EDGE,"E161")])],"isStart":false});
            fillet(context, id + "F31", {"entities" : qUnion([Q0, Q1, Q2, Q3, Q4, Q5, Q6, Q7]), "radius" : 3 * mm, "tangentPropagation" : true, "allowEdgeOverflow" : false});
        }
        {
            var Q0;
            Q0=makeQuery(id+"F29.imprint","IMPRINT",FACE,{"disambiguationData":[TD([[makeQuery(id+"F29.imprint","IMPRINT",EDGE,{"derivedFrom":sQuery(id+"F29.wireOp",EDGE,"E164")}),1.0]])]});
            extrude(context, id + "F32", {"entities" : qUnion([Q0]), "operationType" : NewBodyOperationType.REMOVE, "oppositeDirection" : true, "depth" : 25 * mm, "offsetDistance" : 25 * mm});
        }
        {
            var Q0;
            {var subQ0=sQuery(id+"F0.wireOp",EDGE,"E0.bottom");Q0=makeQuery(id+"F2.boolean.opBoolean","MERGE",FACE,{"derivedFrom":[makeQuery(id+"F1.opExtrude","SWEPT_FACE",FACE,{"disambiguationData":[OSD([subQ0])]}),makeQuery(id+"F2.opExtrude","SWEPT_FACE",FACE,{"disambiguationData":[OSD([subQ0])]})]});}
            var sketch = newSketch(context, id + "F33", { "sketchPlane" : qUnion([Q0])});
            skText(sketch, "E166", { "text": "Ivan Yevchyk", "fontName": "OpenSans-Bold.ttf"});
            const initialGuessF33  = {"E166": [-0.0575, 0.01, 1, 0, 0.01249]};
            skSetInitialGuess(sketch, initialGuessF33);
            skSolve(sketch);
        }
        {
            var Q0;
            Q0 = qSketchRegion(id + "F33", true);
            extrude(context, id + "F34", {"entities" : qUnion([Q0]), "operationType" : NewBodyOperationType.ADD, "depth" : 1 * mm, "offsetDistance" : 25 * mm});
        }
    });